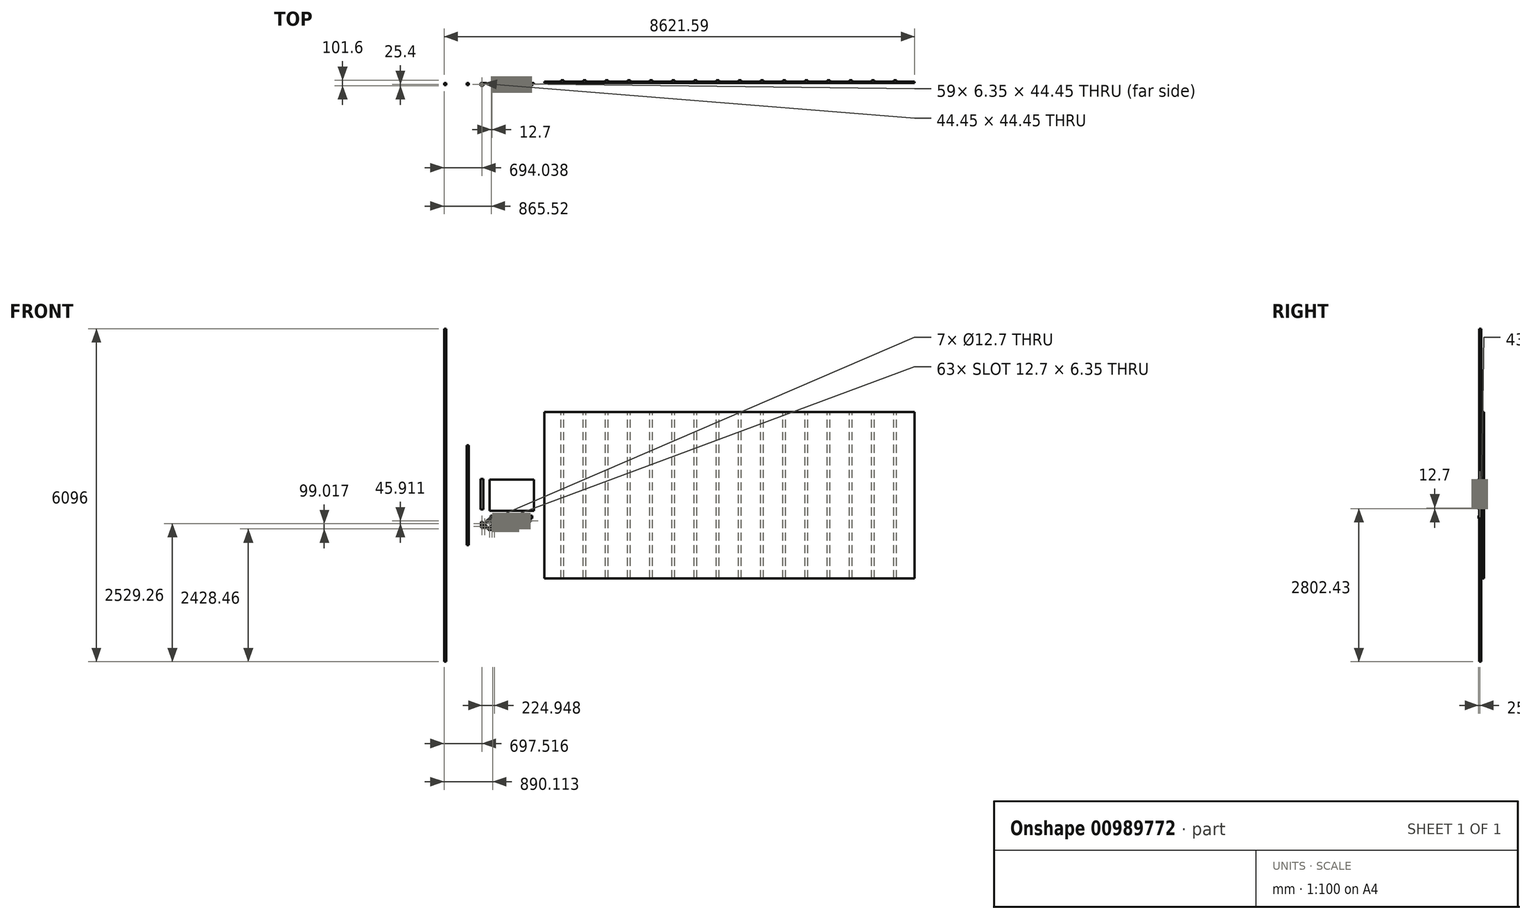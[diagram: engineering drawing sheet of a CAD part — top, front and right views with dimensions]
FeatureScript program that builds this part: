
annotation { "Feature Type Name" : "Feature", "Feature Type Description" : "" }
export const myFeature = defineFeature(function(context is Context, id is Id, definition is map)
    precondition{}
    {
        {
            var Q0;
            Q0=qCreatedBy(makeId("Front.planeOp"),FACE);
            var sketch = newSketch(context, id + "F0", { "sketchPlane" : qUnion([Q0])});
            skLineSegment(sketch, "E0.bottom", {"start": v(-3390.9, -1524) * mm, "end": v(3390.9, -1524) * mm});
            skLineSegment(sketch, "E0.top", {"start": v(-3390.9, 1524) * mm, "end": v(3390.9, 1524) * mm});
            skLineSegment(sketch, "E0.left", {"start": v(-3390.9, -1524) * mm, "end": v(-3390.9, 1524) * mm});
            skLineSegment(sketch, "E0.right", {"start": v(3390.9, -1524) * mm, "end": v(3390.9, 1524) * mm});
            skPoint(sketch, "E0.middle", {"position": v(0, 0) * mm});
            skSolve(sketch);
        }
        {
            var Q0;
            Q0 = qSketchRegion(id + "F0", true);
            extrude(context, id + "F1", {"entities" : qUnion([Q0]), "oppositeDirection" : true, "depth" : 25.4 * mm, "offsetDistance" : 25.4 * mm});
        }
        {
            var Q0;
            Q0=makeQuery(id+"F1.opExtrude","SWEPT_FACE",FACE,{"disambiguationData":[OSD([sQuery(id+"F0.wireOp",EDGE,"E0.top")])]});
            var sketch = newSketch(context, id + "F2", { "sketchPlane" : qUnion([Q0])});
            skLineSegment(sketch, "E1", {"start": v(-3390.9, 25.4) * mm, "end": v(-3086.1, 25.4) * mm});
            skLineSegment(sketch, "E2.bottom", {"start": v(-3086.1, 25.4) * mm, "end": v(-3060.7, 25.4) * mm});
            skLineSegment(sketch, "E2.top", {"start": v(-3086.1, 50.8) * mm, "end": v(-3060.7, 50.8) * mm});
            skLineSegment(sketch, "E2.left", {"start": v(-3086.1, 25.4) * mm, "end": v(-3086.1, 50.8) * mm});
            skLineSegment(sketch, "E2.right", {"start": v(-3060.7, 25.4) * mm, "end": v(-3060.7, 50.8) * mm});
            skLineSegment(sketch, "E3.MirrorCS", {"start": v(-3035.3, 50.8) * mm, "end": v(-3060.7, 50.8) * mm});
            skLineSegment(sketch, "E4.MirrorCS", {"start": v(-3035.3, 25.4) * mm, "end": v(-3035.3, 50.8) * mm});
            skLineSegment(sketch, "E5.MirrorCS", {"start": v(-3035.3, 25.4) * mm, "end": v(-3060.7, 25.4) * mm});
            skLineSegment(sketch, "E6.1.0.0", {"start": v(-2654.3, 25.4) * mm, "end": v(-2654.3, 50.8) * mm});
            skLineSegment(sketch, "E6.1.0.1", {"start": v(-2628.9, 25.4) * mm, "end": v(-2628.9, 50.8) * mm});
            skLineSegment(sketch, "E6.1.0.2", {"start": v(-2628.9, 50.8) * mm, "end": v(-2654.3, 50.8) * mm});
            skLineSegment(sketch, "E6.1.0.3", {"start": v(-2679.7, 50.8) * mm, "end": v(-2654.3, 50.8) * mm});
            skLineSegment(sketch, "E6.1.0.4", {"start": v(-2679.7, 25.4) * mm, "end": v(-2679.7, 50.8) * mm});
            skLineSegment(sketch, "E6.1.0.5", {"start": v(-2679.7, 25.4) * mm, "end": v(-2654.3, 25.4) * mm});
            skLineSegment(sketch, "E6.1.0.6", {"start": v(-2628.9, 25.4) * mm, "end": v(-2654.3, 25.4) * mm});
            skLineSegment(sketch, "E6.2.0.0", {"start": v(-2247.9, 25.4) * mm, "end": v(-2247.9, 50.8) * mm});
            skLineSegment(sketch, "E6.2.0.1", {"start": v(-2222.5, 25.4) * mm, "end": v(-2222.5, 50.8) * mm});
            skLineSegment(sketch, "E6.2.0.2", {"start": v(-2222.5, 50.8) * mm, "end": v(-2247.9, 50.8) * mm});
            skLineSegment(sketch, "E6.2.0.3", {"start": v(-2273.3, 50.8) * mm, "end": v(-2247.9, 50.8) * mm});
            skLineSegment(sketch, "E6.2.0.4", {"start": v(-2273.3, 25.4) * mm, "end": v(-2273.3, 50.8) * mm});
            skLineSegment(sketch, "E6.2.0.5", {"start": v(-2273.3, 25.4) * mm, "end": v(-2247.9, 25.4) * mm});
            skLineSegment(sketch, "E6.2.0.6", {"start": v(-2222.5, 25.4) * mm, "end": v(-2247.9, 25.4) * mm});
            skLineSegment(sketch, "E6.3.0.0", {"start": v(-1841.5, 25.4) * mm, "end": v(-1841.5, 50.8) * mm});
            skLineSegment(sketch, "E6.3.0.1", {"start": v(-1816.1, 25.4) * mm, "end": v(-1816.1, 50.8) * mm});
            skLineSegment(sketch, "E6.3.0.2", {"start": v(-1816.1, 50.8) * mm, "end": v(-1841.5, 50.8) * mm});
            skLineSegment(sketch, "E6.3.0.3", {"start": v(-1866.9, 50.8) * mm, "end": v(-1841.5, 50.8) * mm});
            skLineSegment(sketch, "E6.3.0.4", {"start": v(-1866.9, 25.4) * mm, "end": v(-1866.9, 50.8) * mm});
            skLineSegment(sketch, "E6.3.0.5", {"start": v(-1866.9, 25.4) * mm, "end": v(-1841.5, 25.4) * mm});
            skLineSegment(sketch, "E6.3.0.6", {"start": v(-1816.1, 25.4) * mm, "end": v(-1841.5, 25.4) * mm});
            skLineSegment(sketch, "E6.4.0.0", {"start": v(-1435.1, 25.4) * mm, "end": v(-1435.1, 50.8) * mm});
            skLineSegment(sketch, "E6.4.0.1", {"start": v(-1409.7, 25.4) * mm, "end": v(-1409.7, 50.8) * mm});
            skLineSegment(sketch, "E6.4.0.2", {"start": v(-1409.7, 50.8) * mm, "end": v(-1435.1, 50.8) * mm});
            skLineSegment(sketch, "E6.4.0.3", {"start": v(-1460.5, 50.8) * mm, "end": v(-1435.1, 50.8) * mm});
            skLineSegment(sketch, "E6.4.0.4", {"start": v(-1460.5, 25.4) * mm, "end": v(-1460.5, 50.8) * mm});
            skLineSegment(sketch, "E6.4.0.5", {"start": v(-1460.5, 25.4) * mm, "end": v(-1435.1, 25.4) * mm});
            skLineSegment(sketch, "E6.4.0.6", {"start": v(-1409.7, 25.4) * mm, "end": v(-1435.1, 25.4) * mm});
            skLineSegment(sketch, "E6.5.0.0", {"start": v(-1028.7, 25.4) * mm, "end": v(-1028.7, 50.8) * mm});
            skLineSegment(sketch, "E6.5.0.1", {"start": v(-1003.3, 25.4) * mm, "end": v(-1003.3, 50.8) * mm});
            skLineSegment(sketch, "E6.5.0.2", {"start": v(-1003.3, 50.8) * mm, "end": v(-1028.7, 50.8) * mm});
            skLineSegment(sketch, "E6.5.0.3", {"start": v(-1054.1, 50.8) * mm, "end": v(-1028.7, 50.8) * mm});
            skLineSegment(sketch, "E6.5.0.4", {"start": v(-1054.1, 25.4) * mm, "end": v(-1054.1, 50.8) * mm});
            skLineSegment(sketch, "E6.5.0.5", {"start": v(-1054.1, 25.4) * mm, "end": v(-1028.7, 25.4) * mm});
            skLineSegment(sketch, "E6.5.0.6", {"start": v(-1003.3, 25.4) * mm, "end": v(-1028.7, 25.4) * mm});
            skLineSegment(sketch, "E6.6.0.0", {"start": v(-622.3, 25.4) * mm, "end": v(-622.3, 50.8) * mm});
            skLineSegment(sketch, "E6.6.0.1", {"start": v(-596.9, 25.4) * mm, "end": v(-596.9, 50.8) * mm});
            skLineSegment(sketch, "E6.6.0.2", {"start": v(-596.9, 50.8) * mm, "end": v(-622.3, 50.8) * mm});
            skLineSegment(sketch, "E6.6.0.3", {"start": v(-647.7, 50.8) * mm, "end": v(-622.3, 50.8) * mm});
            skLineSegment(sketch, "E6.6.0.4", {"start": v(-647.7, 25.4) * mm, "end": v(-647.7, 50.8) * mm});
            skLineSegment(sketch, "E6.6.0.5", {"start": v(-647.7, 25.4) * mm, "end": v(-622.3, 25.4) * mm});
            skLineSegment(sketch, "E6.6.0.6", {"start": v(-596.9, 25.4) * mm, "end": v(-622.3, 25.4) * mm});
            skLineSegment(sketch, "E6.7.0.0", {"start": v(-215.9, 25.4) * mm, "end": v(-215.9, 50.8) * mm});
            skLineSegment(sketch, "E6.7.0.1", {"start": v(-190.5, 25.4) * mm, "end": v(-190.5, 50.8) * mm});
            skLineSegment(sketch, "E6.7.0.2", {"start": v(-190.5, 50.8) * mm, "end": v(-215.9, 50.8) * mm});
            skLineSegment(sketch, "E6.7.0.3", {"start": v(-241.3, 50.8) * mm, "end": v(-215.9, 50.8) * mm});
            skLineSegment(sketch, "E6.7.0.4", {"start": v(-241.3, 25.4) * mm, "end": v(-241.3, 50.8) * mm});
            skLineSegment(sketch, "E6.7.0.5", {"start": v(-241.3, 25.4) * mm, "end": v(-215.9, 25.4) * mm});
            skLineSegment(sketch, "E6.7.0.6", {"start": v(-190.5, 25.4) * mm, "end": v(-215.9, 25.4) * mm});
            skLineSegment(sketch, "E6.8.0.0", {"start": v(190.5, 25.4) * mm, "end": v(190.5, 50.8) * mm});
            skLineSegment(sketch, "E6.8.0.1", {"start": v(215.9, 25.4) * mm, "end": v(215.9, 50.8) * mm});
            skLineSegment(sketch, "E6.8.0.2", {"start": v(215.9, 50.8) * mm, "end": v(190.5, 50.8) * mm});
            skLineSegment(sketch, "E6.8.0.3", {"start": v(165.1, 50.8) * mm, "end": v(190.5, 50.8) * mm});
            skLineSegment(sketch, "E6.8.0.4", {"start": v(165.1, 25.4) * mm, "end": v(165.1, 50.8) * mm});
            skLineSegment(sketch, "E6.8.0.5", {"start": v(165.1, 25.4) * mm, "end": v(190.5, 25.4) * mm});
            skLineSegment(sketch, "E6.8.0.6", {"start": v(215.9, 25.4) * mm, "end": v(190.5, 25.4) * mm});
            skLineSegment(sketch, "E6.9.0.0", {"start": v(596.9, 25.4) * mm, "end": v(596.9, 50.8) * mm});
            skLineSegment(sketch, "E6.9.0.1", {"start": v(622.3, 25.4) * mm, "end": v(622.3, 50.8) * mm});
            skLineSegment(sketch, "E6.9.0.2", {"start": v(622.3, 50.8) * mm, "end": v(596.9, 50.8) * mm});
            skLineSegment(sketch, "E6.9.0.3", {"start": v(571.5, 50.8) * mm, "end": v(596.9, 50.8) * mm});
            skLineSegment(sketch, "E6.9.0.4", {"start": v(571.5, 25.4) * mm, "end": v(571.5, 50.8) * mm});
            skLineSegment(sketch, "E6.9.0.5", {"start": v(571.5, 25.4) * mm, "end": v(596.9, 25.4) * mm});
            skLineSegment(sketch, "E6.9.0.6", {"start": v(622.3, 25.4) * mm, "end": v(596.9, 25.4) * mm});
            skLineSegment(sketch, "E6.10.0.0", {"start": v(1003.3, 25.4) * mm, "end": v(1003.3, 50.8) * mm});
            skLineSegment(sketch, "E6.10.0.1", {"start": v(1028.7, 25.4) * mm, "end": v(1028.7, 50.8) * mm});
            skLineSegment(sketch, "E6.10.0.2", {"start": v(1028.7, 50.8) * mm, "end": v(1003.3, 50.8) * mm});
            skLineSegment(sketch, "E6.10.0.3", {"start": v(977.9, 50.8) * mm, "end": v(1003.3, 50.8) * mm});
            skLineSegment(sketch, "E6.10.0.4", {"start": v(977.9, 25.4) * mm, "end": v(977.9, 50.8) * mm});
            skLineSegment(sketch, "E6.10.0.5", {"start": v(977.9, 25.4) * mm, "end": v(1003.3, 25.4) * mm});
            skLineSegment(sketch, "E6.10.0.6", {"start": v(1028.7, 25.4) * mm, "end": v(1003.3, 25.4) * mm});
            skLineSegment(sketch, "E6.11.0.0", {"start": v(1409.7, 25.4) * mm, "end": v(1409.7, 50.8) * mm});
            skLineSegment(sketch, "E6.11.0.1", {"start": v(1435.1, 25.4) * mm, "end": v(1435.1, 50.8) * mm});
            skLineSegment(sketch, "E6.11.0.2", {"start": v(1435.1, 50.8) * mm, "end": v(1409.7, 50.8) * mm});
            skLineSegment(sketch, "E6.11.0.3", {"start": v(1384.3, 50.8) * mm, "end": v(1409.7, 50.8) * mm});
            skLineSegment(sketch, "E6.11.0.4", {"start": v(1384.3, 25.4) * mm, "end": v(1384.3, 50.8) * mm});
            skLineSegment(sketch, "E6.11.0.5", {"start": v(1384.3, 25.4) * mm, "end": v(1409.7, 25.4) * mm});
            skLineSegment(sketch, "E6.11.0.6", {"start": v(1435.1, 25.4) * mm, "end": v(1409.7, 25.4) * mm});
            skLineSegment(sketch, "E6.12.0.0", {"start": v(1816.1, 25.4) * mm, "end": v(1816.1, 50.8) * mm});
            skLineSegment(sketch, "E6.12.0.1", {"start": v(1841.5, 25.4) * mm, "end": v(1841.5, 50.8) * mm});
            skLineSegment(sketch, "E6.12.0.2", {"start": v(1841.5, 50.8) * mm, "end": v(1816.1, 50.8) * mm});
            skLineSegment(sketch, "E6.12.0.3", {"start": v(1790.7, 50.8) * mm, "end": v(1816.1, 50.8) * mm});
            skLineSegment(sketch, "E6.12.0.4", {"start": v(1790.7, 25.4) * mm, "end": v(1790.7, 50.8) * mm});
            skLineSegment(sketch, "E6.12.0.5", {"start": v(1790.7, 25.4) * mm, "end": v(1816.1, 25.4) * mm});
            skLineSegment(sketch, "E6.12.0.6", {"start": v(1841.5, 25.4) * mm, "end": v(1816.1, 25.4) * mm});
            skLineSegment(sketch, "E6.13.0.0", {"start": v(2222.5, 25.4) * mm, "end": v(2222.5, 50.8) * mm});
            skLineSegment(sketch, "E6.13.0.1", {"start": v(2247.9, 25.4) * mm, "end": v(2247.9, 50.8) * mm});
            skLineSegment(sketch, "E6.13.0.2", {"start": v(2247.9, 50.8) * mm, "end": v(2222.5, 50.8) * mm});
            skLineSegment(sketch, "E6.13.0.3", {"start": v(2197.1, 50.8) * mm, "end": v(2222.5, 50.8) * mm});
            skLineSegment(sketch, "E6.13.0.4", {"start": v(2197.1, 25.4) * mm, "end": v(2197.1, 50.8) * mm});
            skLineSegment(sketch, "E6.13.0.5", {"start": v(2197.1, 25.4) * mm, "end": v(2222.5, 25.4) * mm});
            skLineSegment(sketch, "E6.13.0.6", {"start": v(2247.9, 25.4) * mm, "end": v(2222.5, 25.4) * mm});
            skLineSegment(sketch, "E6.14.0.0", {"start": v(2628.9, 25.4) * mm, "end": v(2628.9, 50.8) * mm});
            skLineSegment(sketch, "E6.14.0.1", {"start": v(2654.3, 25.4) * mm, "end": v(2654.3, 50.8) * mm});
            skLineSegment(sketch, "E6.14.0.2", {"start": v(2654.3, 50.8) * mm, "end": v(2628.9, 50.8) * mm});
            skLineSegment(sketch, "E6.14.0.3", {"start": v(2603.5, 50.8) * mm, "end": v(2628.9, 50.8) * mm});
            skLineSegment(sketch, "E6.14.0.4", {"start": v(2603.5, 25.4) * mm, "end": v(2603.5, 50.8) * mm});
            skLineSegment(sketch, "E6.14.0.5", {"start": v(2603.5, 25.4) * mm, "end": v(2628.9, 25.4) * mm});
            skLineSegment(sketch, "E6.14.0.6", {"start": v(2654.3, 25.4) * mm, "end": v(2628.9, 25.4) * mm});
            skLineSegment(sketch, "E6.15.0.0", {"start": v(3035.3, 25.4) * mm, "end": v(3035.3, 50.8) * mm});
            skLineSegment(sketch, "E6.15.0.1", {"start": v(3060.7, 25.4) * mm, "end": v(3060.7, 50.8) * mm});
            skLineSegment(sketch, "E6.15.0.2", {"start": v(3060.7, 50.8) * mm, "end": v(3035.3, 50.8) * mm});
            skLineSegment(sketch, "E6.15.0.3", {"start": v(3009.9, 50.8) * mm, "end": v(3035.3, 50.8) * mm});
            skLineSegment(sketch, "E6.15.0.4", {"start": v(3009.9, 25.4) * mm, "end": v(3009.9, 50.8) * mm});
            skLineSegment(sketch, "E6.15.0.5", {"start": v(3009.9, 25.4) * mm, "end": v(3035.3, 25.4) * mm});
            skLineSegment(sketch, "E6.15.0.6", {"start": v(3060.7, 25.4) * mm, "end": v(3035.3, 25.4) * mm});
            skLineSegment(sketch, "E6.direction1", {"start": v(-3060.7, 25.4) * mm, "end": v(-2654.3, 25.4) * mm, "construction": true});
            skSolve(sketch);
        }
        {
            var Q0;
            Q0 = qSketchRegion(id + "F2", true);
            extrude(context, id + "F3", {"entities" : qUnion([Q0]), "operationType" : NewBodyOperationType.ADD, "oppositeDirection" : true, "depth" : 3048 * mm, "offsetDistance" : 25.4 * mm});
        }
        {
            var Q0;
            Q0=makeQuery(id+"F1.opExtrude","CAP_FACE",FACE,{"disambiguationData":[OSD([sQuery(id+"F0.wireOp",EDGE,"E0.bottom"),sQuery(id+"F0.wireOp",EDGE,"E0.top"),sQuery(id+"F0.wireOp",EDGE,"E0.left"),sQuery(id+"F0.wireOp",EDGE,"E0.right")])],"isStart":true});
            var sketch = newSketch(context, id + "F4", { "sketchPlane" : qUnion([Q0])});
            skLineSegment(sketch, "E7.bottom", {"start": v(-4398.38, -285.75) * mm, "end": v(-3585.58, -285.75) * mm});
            skLineSegment(sketch, "E7.top", {"start": v(-4398.38, 285.75) * mm, "end": v(-3585.58, 285.75) * mm});
            skLineSegment(sketch, "E7.left", {"start": v(-4398.38, -285.75) * mm, "end": v(-4398.38, 285.75) * mm});
            skLineSegment(sketch, "E7.right", {"start": v(-3585.58, -285.75) * mm, "end": v(-3585.58, 285.75) * mm});
            skPoint(sketch, "E7.middle", {"position": v(-3991.98, 0) * mm});
            skSolve(sketch);
        }
        {
            var Q0;
            Q0 = qSketchRegion(id + "F4", true);
            extrude(context, id + "F5", {"entities" : qUnion([Q0]), "depth" : 3.17 * mm, "offsetDistance" : 25.4 * mm});
        }
        {
            var Q0;
            Q0=makeQuery(id+"F1.opExtrude","CAP_FACE",FACE,{"disambiguationData":[OSD([sQuery(id+"F0.wireOp",EDGE,"E0.bottom"),sQuery(id+"F0.wireOp",EDGE,"E0.top"),sQuery(id+"F0.wireOp",EDGE,"E0.left"),sQuery(id+"F0.wireOp",EDGE,"E0.right")])],"isStart":true});
            var sketch = newSketch(context, id + "F6", { "sketchPlane" : qUnion([Q0])});
            skLineSegment(sketch, "E8.bottom", {"start": v(-4775.55, -914.4) * mm, "end": v(-4813.65, -914.4) * mm});
            skLineSegment(sketch, "E8.top", {"start": v(-4775.55, 914.4) * mm, "end": v(-4813.65, 914.4) * mm});
            skLineSegment(sketch, "E8.left", {"start": v(-4775.55, -914.4) * mm, "end": v(-4775.55, 914.4) * mm});
            skLineSegment(sketch, "E8.right", {"start": v(-4813.65, -914.4) * mm, "end": v(-4813.65, 914.4) * mm});
            skPoint(sketch, "E8.middle", {"position": v(-4794.6, 0) * mm});
            skLineSegment(sketch, "E9.bottom", {"start": v(-5192.6, -3048) * mm, "end": v(-5230.7, -3048) * mm});
            skLineSegment(sketch, "E9.top", {"start": v(-5192.6, 3048) * mm, "end": v(-5230.7, 3048) * mm});
            skLineSegment(sketch, "E9.left", {"start": v(-5192.6, -3048) * mm, "end": v(-5192.6, 3048) * mm});
            skLineSegment(sketch, "E9.right", {"start": v(-5230.7, -3048) * mm, "end": v(-5230.7, 3048) * mm});
            skPoint(sketch, "E9.middle", {"position": v(-5211.64, 0) * mm});
            skSolve(sketch);
        }
        {
            var Q0;
            Q0 = qSketchRegion(id + "F6", true);
            extrude(context, id + "F7", {"entities" : qUnion([Q0]), "depth" : 38.1 * mm, "offsetDistance" : 25.4 * mm});
        }
        {
            var Q0;
            Q0=makeQuery(id+"F1.opExtrude","CAP_FACE",FACE,{"disambiguationData":[OSD([sQuery(id+"F0.wireOp",EDGE,"E0.bottom"),sQuery(id+"F0.wireOp",EDGE,"E0.top"),sQuery(id+"F0.wireOp",EDGE,"E0.left"),sQuery(id+"F0.wireOp",EDGE,"E0.right")])],"isStart":true});
            var sketch = newSketch(context, id + "F8", { "sketchPlane" : qUnion([Q0])});
            skLineSegment(sketch, "E10.bottom", {"start": v(-4514.12, -590.37) * mm, "end": v(-4552.22, -590.37) * mm});
            skLineSegment(sketch, "E10.top", {"start": v(-4514.12, -488.77) * mm, "end": v(-4552.22, -488.77) * mm});
            skLineSegment(sketch, "E10.left", {"start": v(-4514.12, -590.37) * mm, "end": v(-4514.12, -488.77) * mm});
            skLineSegment(sketch, "E10.right", {"start": v(-4552.22, -590.37) * mm, "end": v(-4552.22, -488.77) * mm});
            skPoint(sketch, "E10.middle", {"position": v(-4533.17, -539.57) * mm});
            skLineSegment(sketch, "E11.bottom", {"start": v(-4282.83, -638.59) * mm, "end": v(-4422.53, -638.59) * mm});
            skLineSegment(sketch, "E11.top", {"start": v(-4282.83, -600.49) * mm, "end": v(-4422.53, -600.49) * mm});
            skLineSegment(sketch, "E11.left", {"start": v(-4282.83, -638.59) * mm, "end": v(-4282.83, -600.49) * mm});
            skLineSegment(sketch, "E11.right", {"start": v(-4422.53, -638.59) * mm, "end": v(-4422.53, -600.49) * mm});
            skPoint(sketch, "E11.middle", {"position": v(-4352.68, -619.54) * mm});
            skLineSegment(sketch, "E12.bottom", {"start": v(-4552.22, -590.37) * mm, "end": v(-4450.62, -590.37) * mm});
            skLineSegment(sketch, "E12.top", {"start": v(-4552.22, -552.27) * mm, "end": v(-4450.62, -552.27) * mm});
            skLineSegment(sketch, "E12.left", {"start": v(-4552.22, -590.37) * mm, "end": v(-4552.22, -552.27) * mm});
            skLineSegment(sketch, "E12.right", {"start": v(-4450.62, -590.37) * mm, "end": v(-4450.62, -552.27) * mm});
            skLineSegment(sketch, "E13.bottom", {"start": v(-4371.73, -638.59) * mm, "end": v(-4333.63, -638.59) * mm});
            skLineSegment(sketch, "E13.top", {"start": v(-4371.73, -549.69) * mm, "end": v(-4333.63, -549.69) * mm});
            skLineSegment(sketch, "E13.left", {"start": v(-4371.73, -638.59) * mm, "end": v(-4371.73, -549.69) * mm});
            skLineSegment(sketch, "E13.right", {"start": v(-4333.63, -638.59) * mm, "end": v(-4333.63, -549.69) * mm});
            skPoint(sketch, "E13.middle", {"position": v(-4352.68, -594.14) * mm});
            skSolve(sketch);
        }
        {
            var Q0;
            {var subQ0=sQuery(id+"F8.wireOp",EDGE,"E13.left");var subQ1=sQuery(id+"F8.wireOp",EDGE,"E11.bottom");var subQ2=makeQuery(id+"F8.imprint","INTERSECT",VERTEX,{"derivedFrom":[subQ1,subQ0]});var subQ11=sQuery(id+"F8.wireOp",EDGE,"E13.top");var subQ12=sQuery(id+"F8.wireOp",EDGE,"E11.right");var subQ13=sQuery(id+"F8.wireOp",EDGE,"E11.left");var subQ14=sQuery(id+"F8.wireOp",EDGE,"E10.bottom");var subQ18=sQuery(id+"F8.wireOp",EDGE,"E12.bottom");var subQ24=sQuery(id+"F8.wireOp",EDGE,"E10.top");Q0=qUnion([makeQuery(id+"F8.imprint","IMPRINT",FACE,{"disambiguationData":[TD([[makeQuery(id+"F8.imprint","IMPRINT",EDGE,{"derivedFrom":subQ24}),1.0]])]}),makeQuery(id+"F8.imprint","IMPRINT",FACE,{"disambiguationData":[TD([[makeQuery(id+"F8.imprint","IMPRINT",EDGE,{"derivedFrom":subQ18}),1.0]])]}),makeQuery(id+"F8.imprint","IMPRINT",FACE,{"disambiguationData":[TD([[makeQuery(id+"F8.imprint","IMPRINT",EDGE,{"derivedFrom":subQ14}),-1.0]])]}),makeQuery(id+"F8.imprint","IMPRINT",FACE,{"disambiguationData":[TD([[makeQuery(id+"F8.imprint","IMPRINT",EDGE,{"derivedFrom":subQ13}),1.0]])]}),makeQuery(id+"F8.imprint","IMPRINT",FACE,{"disambiguationData":[TD([[makeQuery(id+"F8.imprint","IMPRINT",EDGE,{"derivedFrom":subQ12}),-1.0]])]}),makeQuery(id+"F8.imprint","IMPRINT",FACE,{"disambiguationData":[TD([[makeQuery(id+"F8.imprint","IMPRINT",EDGE,{"derivedFrom":subQ11}),-1.0]])]}),makeQuery(id+"F8.imprint","IMPRINT",FACE,{"disambiguationData":[TD([[makeQuery(id+"F8.imprint","IMPRINT",EDGE,{"disambiguationData":[TD([[subQ2,1.0]])],"derivedFrom":subQ1}),-1.0]])]})]);}
            extrude(context, id + "F9", {"entities" : qUnion([Q0]), "depth" : 6.35 * mm, "offsetDistance" : 25.4 * mm});
        }
        {
            var Q0;
            Q0=makeQuery(id+"F9.opExtrude","CAP_FACE",FACE,{"disambiguationData":[OSD([sQuery(id+"F8.wireOp",EDGE,"E10.bottom"),sQuery(id+"F8.wireOp",EDGE,"E10.top"),sQuery(id+"F8.wireOp",EDGE,"E10.left"),sQuery(id+"F8.wireOp",EDGE,"E10.right"),sQuery(id+"F8.wireOp",EDGE,"E12.bottom"),sQuery(id+"F8.wireOp",EDGE,"E12.top"),sQuery(id+"F8.wireOp",EDGE,"E12.right")])],"isStart":false});
            var sketch = newSketch(context, id + "F10", { "sketchPlane" : qUnion([Q0])});
            skLineSegment(sketch, "E14", {"start": v(-4552.22, -590.37) * mm, "end": v(-4514.12, -552.27) * mm});
            skLineSegment(sketch, "E15", {"start": v(-4450.62, -571.32) * mm, "end": v(-4552.22, -571.32) * mm});
            skLineSegment(sketch, "E16", {"start": v(-4533.17, -488.77) * mm, "end": v(-4533.17, -590.37) * mm});
            skCircle(sketch, "E17", {"center": v(-4533.17, -520.52) * mm, "radius": 6.35 * mm});
            skPoint(sketch, "E17.centerSnap0", {"position": v(-4514.12, -520.52) * mm});
            skCircle(sketch, "E18", {"center": v(-4482.37, -571.32) * mm, "radius": 6.35 * mm});
            skPoint(sketch, "E18.centerSnap0", {"position": v(-4482.37, -552.27) * mm});
            skCircle(sketch, "E19", {"center": v(-4533.17, -571.32) * mm, "radius": 6.35 * mm});
            skSolve(sketch);
        }
        {
            var Q0;
            Q0 = qSketchRegion(id + "F10", true);
            extrude(context, id + "F11", {"entities" : qUnion([Q0]), "operationType" : NewBodyOperationType.REMOVE, "oppositeDirection" : true, "depth" : 25.4 * mm, "offsetDistance" : 25.4 * mm});
        }
        {
            var Q0;
            Q0=makeQuery(id+"F9.opExtrude","CAP_FACE",FACE,{"disambiguationData":[OSD([sQuery(id+"F8.wireOp",EDGE,"E11.bottom"),sQuery(id+"F8.wireOp",EDGE,"E11.top"),sQuery(id+"F8.wireOp",EDGE,"E11.left"),sQuery(id+"F8.wireOp",EDGE,"E11.right"),sQuery(id+"F8.wireOp",EDGE,"E13.top"),sQuery(id+"F8.wireOp",EDGE,"E13.left"),sQuery(id+"F8.wireOp",EDGE,"E13.right")])],"isStart":false});
            var sketch = newSketch(context, id + "F12", { "sketchPlane" : qUnion([Q0])});
            skCircle(sketch, "E20", {"center": v(-4352.68, -575.09) * mm, "radius": 6.35 * mm});
            skPoint(sketch, "E20.centerSnap0", {"position": v(-4352.68, -549.69) * mm});
            skPoint(sketch, "E20.centerSnap1", {"position": v(-4371.73, -575.09) * mm});
            skCircle(sketch, "E21", {"center": v(-4397.13, -619.54) * mm, "radius": 6.35 * mm});
            skPoint(sketch, "E21.centerSnap0", {"position": v(-4422.53, -619.54) * mm});
            skPoint(sketch, "E21.centerSnap1", {"position": v(-4397.13, -600.49) * mm});
            skCircle(sketch, "E22", {"center": v(-4308.23, -619.54) * mm, "radius": 6.35 * mm});
            skPoint(sketch, "E22.centerSnap0", {"position": v(-4282.83, -619.54) * mm});
            skPoint(sketch, "E22.centerSnap1", {"position": v(-4308.23, -600.49) * mm});
            skCircle(sketch, "E23", {"center": v(-4352.68, -619.54) * mm, "radius": 6.35 * mm});
            skPoint(sketch, "E23.centerSnap0", {"position": v(-4352.68, -638.59) * mm});
            skSolve(sketch);
        }
        {
            var Q0;
            Q0 = qSketchRegion(id + "F12", true);
            extrude(context, id + "F13", {"entities" : qUnion([Q0]), "operationType" : NewBodyOperationType.REMOVE, "oppositeDirection" : true, "depth" : 25.4 * mm, "offsetDistance" : 25.4 * mm});
        }
        {
            var Q0;
            Q0=makeQuery(id+"F1.opExtrude","CAP_FACE",FACE,{"disambiguationData":[OSD([sQuery(id+"F0.wireOp",EDGE,"E0.bottom"),sQuery(id+"F0.wireOp",EDGE,"E0.top"),sQuery(id+"F0.wireOp",EDGE,"E0.left"),sQuery(id+"F0.wireOp",EDGE,"E0.right")])],"isStart":true});
            var sketch = newSketch(context, id + "F14", { "sketchPlane" : qUnion([Q0])});
            skLineSegment(sketch, "E24.bottom", {"start": v(-4374.7, -372.24) * mm, "end": v(-3612.7, -372.24) * mm});
            skLineSegment(sketch, "E24.top", {"start": v(-4374.7, -423.04) * mm, "end": v(-3612.7, -423.04) * mm});
            skLineSegment(sketch, "E24.left", {"start": v(-4374.7, -372.24) * mm, "end": v(-4374.7, -423.04) * mm});
            skLineSegment(sketch, "E24.right", {"start": v(-3612.7, -372.24) * mm, "end": v(-3612.7, -423.04) * mm});
            skLineSegment(sketch, "E25.bottom", {"start": v(-4562.05, 297.36) * mm, "end": v(-4511.25, 297.36) * mm});
            skLineSegment(sketch, "E25.top", {"start": v(-4562.05, -261.44) * mm, "end": v(-4511.25, -261.44) * mm});
            skLineSegment(sketch, "E25.left", {"start": v(-4562.05, 297.36) * mm, "end": v(-4562.05, -261.44) * mm});
            skLineSegment(sketch, "E25.right", {"start": v(-4511.25, 297.36) * mm, "end": v(-4511.25, -261.44) * mm});
            skSolve(sketch);
        }
        {
            var Q0;
            Q0 = qSketchRegion(id + "F14", true);
            extrude(context, id + "F15", {"entities" : qUnion([Q0]), "depth" : 50.8 * mm, "offsetDistance" : 25.4 * mm});
        }
        {
            var Q0;
            Q0=makeQuery(id+"F15.opExtrude","SWEPT_FACE",FACE,{"disambiguationData":[OSD([sQuery(id+"F14.wireOp",EDGE,"E25.bottom")])]});
            var sketch = newSketch(context, id + "F16", { "sketchPlane" : qUnion([Q0])});
            skLineSegment(sketch, "E26.bottom", {"start": v(-4558.88, -3.18) * mm, "end": v(-4514.43, -3.18) * mm});
            skLineSegment(sketch, "E26.top", {"start": v(-4558.88, -47.63) * mm, "end": v(-4514.43, -47.63) * mm});
            skLineSegment(sketch, "E26.left", {"start": v(-4558.88, -3.18) * mm, "end": v(-4558.88, -47.63) * mm});
            skLineSegment(sketch, "E26.right", {"start": v(-4514.43, -3.18) * mm, "end": v(-4514.43, -47.63) * mm});
            skSolve(sketch);
        }
        {
            var Q0;
            Q0 = qSketchRegion(id + "F16", true);
            extrude(context, id + "F17", {"entities" : qUnion([Q0]), "operationType" : NewBodyOperationType.REMOVE, "oppositeDirection" : true, "depth" : 558.8 * mm, "offsetDistance" : 25.4 * mm});
        }
        {
            var Q0;
            Q0=makeQuery(id+"F15.opExtrude","SWEPT_FACE",FACE,{"disambiguationData":[OSD([sQuery(id+"F14.wireOp",EDGE,"E25.left")])]});
            var sketch = newSketch(context, id + "F18", { "sketchPlane" : qUnion([Q0])});
            skLineSegment(sketch, "E27.bottom", {"start": v(47.62, 291) * mm, "end": v(3.17, 291) * mm});
            skLineSegment(sketch, "E27.top", {"start": v(47.62, 284.66) * mm, "end": v(3.18, 284.66) * mm});
            skLineSegment(sketch, "E27.left", {"start": v(47.62, 284.66) * mm, "end": v(47.62, 291) * mm});
            skLineSegment(sketch, "E27.right", {"start": v(3.17, 284.66) * mm, "end": v(3.17, 291) * mm});
            skLineSegment(sketch, "E28.1.0.0", {"start": v(47.62, 271.96) * mm, "end": v(47.62, 278.3) * mm});
            skLineSegment(sketch, "E28.1.0.1", {"start": v(47.62, 271.96) * mm, "end": v(3.18, 271.96) * mm});
            skLineSegment(sketch, "E28.1.0.2", {"start": v(47.62, 278.3) * mm, "end": v(3.17, 278.3) * mm});
            skLineSegment(sketch, "E28.1.0.3", {"start": v(3.17, 271.96) * mm, "end": v(3.17, 278.3) * mm});
            skLineSegment(sketch, "E28.2.0.0", {"start": v(47.62, 259.26) * mm, "end": v(47.62, 265.6) * mm});
            skLineSegment(sketch, "E28.2.0.1", {"start": v(47.62, 259.26) * mm, "end": v(3.18, 259.26) * mm});
            skLineSegment(sketch, "E28.2.0.2", {"start": v(47.62, 265.6) * mm, "end": v(3.17, 265.6) * mm});
            skLineSegment(sketch, "E28.2.0.3", {"start": v(3.17, 259.26) * mm, "end": v(3.17, 265.6) * mm});
            skLineSegment(sketch, "E28.3.0.0", {"start": v(47.62, 246.56) * mm, "end": v(47.62, 252.9) * mm});
            skLineSegment(sketch, "E28.3.0.1", {"start": v(47.63, 246.56) * mm, "end": v(3.18, 246.56) * mm});
            skLineSegment(sketch, "E28.3.0.2", {"start": v(47.63, 252.9) * mm, "end": v(3.17, 252.9) * mm});
            skLineSegment(sketch, "E28.3.0.3", {"start": v(3.17, 246.56) * mm, "end": v(3.17, 252.9) * mm});
            skLineSegment(sketch, "E28.4.0.0", {"start": v(47.63, 233.86) * mm, "end": v(47.63, 240.2) * mm});
            skLineSegment(sketch, "E28.4.0.1", {"start": v(47.63, 233.86) * mm, "end": v(3.18, 233.86) * mm});
            skLineSegment(sketch, "E28.4.0.2", {"start": v(47.63, 240.2) * mm, "end": v(3.18, 240.2) * mm});
            skLineSegment(sketch, "E28.4.0.3", {"start": v(3.17, 233.86) * mm, "end": v(3.17, 240.2) * mm});
            skLineSegment(sketch, "E28.5.0.0", {"start": v(47.63, 221.16) * mm, "end": v(47.63, 227.5) * mm});
            skLineSegment(sketch, "E28.5.0.1", {"start": v(47.63, 221.16) * mm, "end": v(3.18, 221.16) * mm});
            skLineSegment(sketch, "E28.5.0.2", {"start": v(47.63, 227.5) * mm, "end": v(3.18, 227.5) * mm});
            skLineSegment(sketch, "E28.5.0.3", {"start": v(3.18, 221.16) * mm, "end": v(3.18, 227.5) * mm});
            skLineSegment(sketch, "E28.6.0.0", {"start": v(47.63, 208.46) * mm, "end": v(47.63, 214.8) * mm});
            skLineSegment(sketch, "E28.6.0.1", {"start": v(47.63, 208.46) * mm, "end": v(3.18, 208.46) * mm});
            skLineSegment(sketch, "E28.6.0.2", {"start": v(47.63, 214.8) * mm, "end": v(3.18, 214.8) * mm});
            skLineSegment(sketch, "E28.6.0.3", {"start": v(3.18, 208.46) * mm, "end": v(3.18, 214.8) * mm});
            skLineSegment(sketch, "E28.7.0.0", {"start": v(47.63, 195.76) * mm, "end": v(47.63, 202.1) * mm});
            skLineSegment(sketch, "E28.7.0.1", {"start": v(47.63, 195.76) * mm, "end": v(3.18, 195.76) * mm});
            skLineSegment(sketch, "E28.7.0.2", {"start": v(47.63, 202.1) * mm, "end": v(3.18, 202.1) * mm});
            skLineSegment(sketch, "E28.7.0.3", {"start": v(3.18, 195.76) * mm, "end": v(3.18, 202.1) * mm});
            skLineSegment(sketch, "E28.8.0.0", {"start": v(47.63, 183.06) * mm, "end": v(47.63, 189.4) * mm});
            skLineSegment(sketch, "E28.8.0.1", {"start": v(47.63, 183.06) * mm, "end": v(3.18, 183.06) * mm});
            skLineSegment(sketch, "E28.8.0.2", {"start": v(47.63, 189.4) * mm, "end": v(3.18, 189.4) * mm});
            skLineSegment(sketch, "E28.8.0.3", {"start": v(3.18, 183.06) * mm, "end": v(3.18, 189.4) * mm});
            skLineSegment(sketch, "E28.9.0.0", {"start": v(47.63, 170.36) * mm, "end": v(47.63, 176.7) * mm});
            skLineSegment(sketch, "E28.9.0.1", {"start": v(47.63, 170.36) * mm, "end": v(3.18, 170.36) * mm});
            skLineSegment(sketch, "E28.9.0.2", {"start": v(47.63, 176.7) * mm, "end": v(3.18, 176.7) * mm});
            skLineSegment(sketch, "E28.9.0.3", {"start": v(3.18, 170.36) * mm, "end": v(3.18, 176.7) * mm});
            skLineSegment(sketch, "E28.10.0.0", {"start": v(47.63, 157.66) * mm, "end": v(47.63, 164) * mm});
            skLineSegment(sketch, "E28.10.0.1", {"start": v(47.63, 157.66) * mm, "end": v(3.18, 157.66) * mm});
            skLineSegment(sketch, "E28.10.0.2", {"start": v(47.63, 164) * mm, "end": v(3.18, 164) * mm});
            skLineSegment(sketch, "E28.10.0.3", {"start": v(3.18, 157.66) * mm, "end": v(3.18, 164) * mm});
            skLineSegment(sketch, "E28.11.0.0", {"start": v(47.63, 144.96) * mm, "end": v(47.63, 151.3) * mm});
            skLineSegment(sketch, "E28.11.0.1", {"start": v(47.63, 144.96) * mm, "end": v(3.18, 144.96) * mm});
            skLineSegment(sketch, "E28.11.0.2", {"start": v(47.63, 151.3) * mm, "end": v(3.18, 151.3) * mm});
            skLineSegment(sketch, "E28.11.0.3", {"start": v(3.18, 144.96) * mm, "end": v(3.18, 151.3) * mm});
            skLineSegment(sketch, "E28.12.0.0", {"start": v(47.63, 132.26) * mm, "end": v(47.63, 138.6) * mm});
            skLineSegment(sketch, "E28.12.0.1", {"start": v(47.63, 132.26) * mm, "end": v(3.18, 132.26) * mm});
            skLineSegment(sketch, "E28.12.0.2", {"start": v(47.63, 138.6) * mm, "end": v(3.18, 138.6) * mm});
            skLineSegment(sketch, "E28.12.0.3", {"start": v(3.18, 132.26) * mm, "end": v(3.18, 138.6) * mm});
            skLineSegment(sketch, "E28.13.0.0", {"start": v(47.63, 119.56) * mm, "end": v(47.63, 125.9) * mm});
            skLineSegment(sketch, "E28.13.0.1", {"start": v(47.63, 119.56) * mm, "end": v(3.18, 119.56) * mm});
            skLineSegment(sketch, "E28.13.0.2", {"start": v(47.63, 125.9) * mm, "end": v(3.18, 125.9) * mm});
            skLineSegment(sketch, "E28.13.0.3", {"start": v(3.18, 119.56) * mm, "end": v(3.18, 125.9) * mm});
            skLineSegment(sketch, "E28.14.0.0", {"start": v(47.63, 106.86) * mm, "end": v(47.63, 113.2) * mm});
            skLineSegment(sketch, "E28.14.0.1", {"start": v(47.63, 106.86) * mm, "end": v(3.18, 106.86) * mm});
            skLineSegment(sketch, "E28.14.0.2", {"start": v(47.63, 113.2) * mm, "end": v(3.18, 113.2) * mm});
            skLineSegment(sketch, "E28.14.0.3", {"start": v(3.18, 106.86) * mm, "end": v(3.18, 113.2) * mm});
            skLineSegment(sketch, "E28.15.0.0", {"start": v(47.63, 94.16) * mm, "end": v(47.63, 100.5) * mm});
            skLineSegment(sketch, "E28.15.0.1", {"start": v(47.63, 94.16) * mm, "end": v(3.18, 94.16) * mm});
            skLineSegment(sketch, "E28.15.0.2", {"start": v(47.63, 100.5) * mm, "end": v(3.18, 100.5) * mm});
            skLineSegment(sketch, "E28.15.0.3", {"start": v(3.18, 94.16) * mm, "end": v(3.18, 100.5) * mm});
            skLineSegment(sketch, "E28.16.0.0", {"start": v(47.63, 81.46) * mm, "end": v(47.63, 87.8) * mm});
            skLineSegment(sketch, "E28.16.0.1", {"start": v(47.63, 81.46) * mm, "end": v(3.18, 81.46) * mm});
            skLineSegment(sketch, "E28.16.0.2", {"start": v(47.63, 87.8) * mm, "end": v(3.18, 87.8) * mm});
            skLineSegment(sketch, "E28.16.0.3", {"start": v(3.18, 81.46) * mm, "end": v(3.18, 87.8) * mm});
            skLineSegment(sketch, "E28.17.0.0", {"start": v(47.63, 68.76) * mm, "end": v(47.63, 75.1) * mm});
            skLineSegment(sketch, "E28.17.0.1", {"start": v(47.63, 68.76) * mm, "end": v(3.18, 68.76) * mm});
            skLineSegment(sketch, "E28.17.0.2", {"start": v(47.63, 75.1) * mm, "end": v(3.18, 75.1) * mm});
            skLineSegment(sketch, "E28.17.0.3", {"start": v(3.18, 68.76) * mm, "end": v(3.18, 75.1) * mm});
            skLineSegment(sketch, "E28.18.0.0", {"start": v(47.63, 56.06) * mm, "end": v(47.63, 62.4) * mm});
            skLineSegment(sketch, "E28.18.0.1", {"start": v(47.63, 56.06) * mm, "end": v(3.18, 56.06) * mm});
            skLineSegment(sketch, "E28.18.0.2", {"start": v(47.63, 62.4) * mm, "end": v(3.18, 62.4) * mm});
            skLineSegment(sketch, "E28.18.0.3", {"start": v(3.18, 56.06) * mm, "end": v(3.18, 62.4) * mm});
            skLineSegment(sketch, "E28.19.0.0", {"start": v(47.63, 43.36) * mm, "end": v(47.63, 49.7) * mm});
            skLineSegment(sketch, "E28.19.0.1", {"start": v(47.63, 43.36) * mm, "end": v(3.18, 43.36) * mm});
            skLineSegment(sketch, "E28.19.0.2", {"start": v(47.63, 49.7) * mm, "end": v(3.18, 49.7) * mm});
            skLineSegment(sketch, "E28.19.0.3", {"start": v(3.18, 43.36) * mm, "end": v(3.18, 49.7) * mm});
            skLineSegment(sketch, "E28.20.0.0", {"start": v(47.63, 30.66) * mm, "end": v(47.63, 37) * mm});
            skLineSegment(sketch, "E28.20.0.1", {"start": v(47.63, 30.66) * mm, "end": v(3.18, 30.66) * mm});
            skLineSegment(sketch, "E28.20.0.2", {"start": v(47.63, 37) * mm, "end": v(3.18, 37) * mm});
            skLineSegment(sketch, "E28.20.0.3", {"start": v(3.18, 30.66) * mm, "end": v(3.18, 37) * mm});
            skLineSegment(sketch, "E28.21.0.0", {"start": v(47.63, 17.96) * mm, "end": v(47.63, 24.3) * mm});
            skLineSegment(sketch, "E28.21.0.1", {"start": v(47.63, 17.96) * mm, "end": v(3.18, 17.96) * mm});
            skLineSegment(sketch, "E28.21.0.2", {"start": v(47.63, 24.3) * mm, "end": v(3.18, 24.3) * mm});
            skLineSegment(sketch, "E28.21.0.3", {"start": v(3.18, 17.96) * mm, "end": v(3.18, 24.3) * mm});
            skLineSegment(sketch, "E28.22.0.0", {"start": v(47.63, 5.26) * mm, "end": v(47.63, 11.6) * mm});
            skLineSegment(sketch, "E28.22.0.1", {"start": v(47.63, 5.26) * mm, "end": v(3.18, 5.26) * mm});
            skLineSegment(sketch, "E28.22.0.2", {"start": v(47.63, 11.6) * mm, "end": v(3.18, 11.6) * mm});
            skLineSegment(sketch, "E28.22.0.3", {"start": v(3.18, 5.26) * mm, "end": v(3.18, 11.6) * mm});
            skLineSegment(sketch, "E28.23.0.0", {"start": v(47.63, -7.44) * mm, "end": v(47.63, -1.1) * mm});
            skLineSegment(sketch, "E28.23.0.1", {"start": v(47.63, -7.44) * mm, "end": v(3.18, -7.44) * mm});
            skLineSegment(sketch, "E28.23.0.2", {"start": v(47.63, -1.1) * mm, "end": v(3.18, -1.1) * mm});
            skLineSegment(sketch, "E28.23.0.3", {"start": v(3.18, -7.44) * mm, "end": v(3.18, -1.1) * mm});
            skLineSegment(sketch, "E28.24.0.0", {"start": v(47.63, -20.14) * mm, "end": v(47.63, -13.8) * mm});
            skLineSegment(sketch, "E28.24.0.1", {"start": v(47.63, -20.14) * mm, "end": v(3.18, -20.14) * mm});
            skLineSegment(sketch, "E28.24.0.2", {"start": v(47.63, -13.8) * mm, "end": v(3.18, -13.8) * mm});
            skLineSegment(sketch, "E28.24.0.3", {"start": v(3.18, -20.14) * mm, "end": v(3.18, -13.8) * mm});
            skLineSegment(sketch, "E28.25.0.0", {"start": v(47.63, -32.84) * mm, "end": v(47.63, -26.5) * mm});
            skLineSegment(sketch, "E28.25.0.1", {"start": v(47.63, -32.84) * mm, "end": v(3.18, -32.84) * mm});
            skLineSegment(sketch, "E28.25.0.2", {"start": v(47.63, -26.5) * mm, "end": v(3.18, -26.5) * mm});
            skLineSegment(sketch, "E28.25.0.3", {"start": v(3.18, -32.84) * mm, "end": v(3.18, -26.5) * mm});
            skLineSegment(sketch, "E28.26.0.0", {"start": v(47.63, -45.54) * mm, "end": v(47.63, -39.2) * mm});
            skLineSegment(sketch, "E28.26.0.1", {"start": v(47.63, -45.54) * mm, "end": v(3.18, -45.54) * mm});
            skLineSegment(sketch, "E28.26.0.2", {"start": v(47.63, -39.2) * mm, "end": v(3.18, -39.2) * mm});
            skLineSegment(sketch, "E28.26.0.3", {"start": v(3.18, -45.54) * mm, "end": v(3.18, -39.2) * mm});
            skLineSegment(sketch, "E28.27.0.0", {"start": v(47.63, -58.24) * mm, "end": v(47.63, -51.9) * mm});
            skLineSegment(sketch, "E28.27.0.1", {"start": v(47.63, -58.24) * mm, "end": v(3.18, -58.24) * mm});
            skLineSegment(sketch, "E28.27.0.2", {"start": v(47.63, -51.9) * mm, "end": v(3.18, -51.9) * mm});
            skLineSegment(sketch, "E28.27.0.3", {"start": v(3.18, -58.24) * mm, "end": v(3.18, -51.9) * mm});
            skLineSegment(sketch, "E28.28.0.0", {"start": v(47.63, -70.94) * mm, "end": v(47.63, -64.6) * mm});
            skLineSegment(sketch, "E28.28.0.1", {"start": v(47.63, -70.94) * mm, "end": v(3.18, -70.94) * mm});
            skLineSegment(sketch, "E28.28.0.2", {"start": v(47.63, -64.6) * mm, "end": v(3.18, -64.6) * mm});
            skLineSegment(sketch, "E28.28.0.3", {"start": v(3.18, -70.94) * mm, "end": v(3.18, -64.6) * mm});
            skLineSegment(sketch, "E28.29.0.0", {"start": v(47.63, -83.64) * mm, "end": v(47.63, -77.3) * mm});
            skLineSegment(sketch, "E28.29.0.1", {"start": v(47.63, -83.64) * mm, "end": v(3.18, -83.64) * mm});
            skLineSegment(sketch, "E28.29.0.2", {"start": v(47.63, -77.3) * mm, "end": v(3.18, -77.3) * mm});
            skLineSegment(sketch, "E28.29.0.3", {"start": v(3.18, -83.64) * mm, "end": v(3.18, -77.3) * mm});
            skLineSegment(sketch, "E28.30.0.0", {"start": v(47.63, -96.34) * mm, "end": v(47.63, -90) * mm});
            skLineSegment(sketch, "E28.30.0.1", {"start": v(47.63, -96.34) * mm, "end": v(3.18, -96.34) * mm});
            skLineSegment(sketch, "E28.30.0.2", {"start": v(47.63, -90) * mm, "end": v(3.18, -90) * mm});
            skLineSegment(sketch, "E28.30.0.3", {"start": v(3.18, -96.34) * mm, "end": v(3.18, -90) * mm});
            skLineSegment(sketch, "E28.31.0.0", {"start": v(47.63, -109.04) * mm, "end": v(47.63, -102.7) * mm});
            skLineSegment(sketch, "E28.31.0.1", {"start": v(47.63, -109.04) * mm, "end": v(3.18, -109.04) * mm});
            skLineSegment(sketch, "E28.31.0.2", {"start": v(47.63, -102.7) * mm, "end": v(3.18, -102.7) * mm});
            skLineSegment(sketch, "E28.31.0.3", {"start": v(3.18, -109.04) * mm, "end": v(3.18, -102.7) * mm});
            skLineSegment(sketch, "E28.32.0.0", {"start": v(47.63, -121.74) * mm, "end": v(47.63, -115.4) * mm});
            skLineSegment(sketch, "E28.32.0.1", {"start": v(47.63, -121.74) * mm, "end": v(3.18, -121.74) * mm});
            skLineSegment(sketch, "E28.32.0.2", {"start": v(47.63, -115.4) * mm, "end": v(3.18, -115.4) * mm});
            skLineSegment(sketch, "E28.32.0.3", {"start": v(3.18, -121.74) * mm, "end": v(3.18, -115.4) * mm});
            skLineSegment(sketch, "E28.33.0.0", {"start": v(47.63, -134.44) * mm, "end": v(47.63, -128.1) * mm});
            skLineSegment(sketch, "E28.33.0.1", {"start": v(47.63, -134.44) * mm, "end": v(3.18, -134.44) * mm});
            skLineSegment(sketch, "E28.33.0.2", {"start": v(47.63, -128.1) * mm, "end": v(3.18, -128.1) * mm});
            skLineSegment(sketch, "E28.33.0.3", {"start": v(3.18, -134.44) * mm, "end": v(3.18, -128.1) * mm});
            skLineSegment(sketch, "E28.34.0.0", {"start": v(47.63, -147.14) * mm, "end": v(47.63, -140.8) * mm});
            skLineSegment(sketch, "E28.34.0.1", {"start": v(47.63, -147.14) * mm, "end": v(3.18, -147.14) * mm});
            skLineSegment(sketch, "E28.34.0.2", {"start": v(47.63, -140.8) * mm, "end": v(3.18, -140.8) * mm});
            skLineSegment(sketch, "E28.34.0.3", {"start": v(3.18, -147.14) * mm, "end": v(3.18, -140.8) * mm});
            skLineSegment(sketch, "E28.35.0.0", {"start": v(47.63, -159.84) * mm, "end": v(47.63, -153.5) * mm});
            skLineSegment(sketch, "E28.35.0.1", {"start": v(47.63, -159.84) * mm, "end": v(3.18, -159.84) * mm});
            skLineSegment(sketch, "E28.35.0.2", {"start": v(47.63, -153.5) * mm, "end": v(3.18, -153.5) * mm});
            skLineSegment(sketch, "E28.35.0.3", {"start": v(3.18, -159.84) * mm, "end": v(3.18, -153.5) * mm});
            skLineSegment(sketch, "E28.36.0.0", {"start": v(47.63, -172.54) * mm, "end": v(47.63, -166.2) * mm});
            skLineSegment(sketch, "E28.36.0.1", {"start": v(47.63, -172.54) * mm, "end": v(3.18, -172.54) * mm});
            skLineSegment(sketch, "E28.36.0.2", {"start": v(47.63, -166.2) * mm, "end": v(3.18, -166.2) * mm});
            skLineSegment(sketch, "E28.36.0.3", {"start": v(3.18, -172.54) * mm, "end": v(3.18, -166.2) * mm});
            skLineSegment(sketch, "E28.37.0.0", {"start": v(47.63, -185.24) * mm, "end": v(47.63, -178.9) * mm});
            skLineSegment(sketch, "E28.37.0.1", {"start": v(47.63, -185.24) * mm, "end": v(3.18, -185.24) * mm});
            skLineSegment(sketch, "E28.37.0.2", {"start": v(47.63, -178.9) * mm, "end": v(3.18, -178.9) * mm});
            skLineSegment(sketch, "E28.37.0.3", {"start": v(3.18, -185.24) * mm, "end": v(3.18, -178.9) * mm});
            skLineSegment(sketch, "E28.38.0.0", {"start": v(47.63, -197.94) * mm, "end": v(47.63, -191.6) * mm});
            skLineSegment(sketch, "E28.38.0.1", {"start": v(47.63, -197.94) * mm, "end": v(3.18, -197.94) * mm});
            skLineSegment(sketch, "E28.38.0.2", {"start": v(47.63, -191.6) * mm, "end": v(3.18, -191.6) * mm});
            skLineSegment(sketch, "E28.38.0.3", {"start": v(3.18, -197.94) * mm, "end": v(3.18, -191.6) * mm});
            skLineSegment(sketch, "E28.39.0.0", {"start": v(47.63, -210.64) * mm, "end": v(47.63, -204.3) * mm});
            skLineSegment(sketch, "E28.39.0.1", {"start": v(47.63, -210.64) * mm, "end": v(3.18, -210.64) * mm});
            skLineSegment(sketch, "E28.39.0.2", {"start": v(47.63, -204.3) * mm, "end": v(3.18, -204.3) * mm});
            skLineSegment(sketch, "E28.39.0.3", {"start": v(3.18, -210.64) * mm, "end": v(3.18, -204.3) * mm});
            skLineSegment(sketch, "E28.direction1", {"start": v(47.62, 284.66) * mm, "end": v(47.62, 271.96) * mm, "construction": true});
            skLineSegment(sketch, "E29.0.40.0", {"start": v(47.63, -223.34) * mm, "end": v(47.63, -217) * mm});
            skLineSegment(sketch, "E29.3.40.0", {"start": v(47.63, -223.34) * mm, "end": v(3.18, -223.34) * mm});
            skLineSegment(sketch, "E29.6.40.0", {"start": v(47.63, -217) * mm, "end": v(3.18, -217) * mm});
            skLineSegment(sketch, "E29.9.40.0", {"start": v(3.18, -223.34) * mm, "end": v(3.18, -217) * mm});
            skLineSegment(sketch, "E30.0.41.0", {"start": v(47.63, -236.04) * mm, "end": v(47.63, -229.7) * mm});
            skLineSegment(sketch, "E30.3.41.0", {"start": v(47.63, -236.04) * mm, "end": v(3.18, -236.04) * mm});
            skLineSegment(sketch, "E30.6.41.0", {"start": v(47.63, -229.7) * mm, "end": v(3.18, -229.7) * mm});
            skLineSegment(sketch, "E30.9.41.0", {"start": v(3.18, -236.04) * mm, "end": v(3.18, -229.7) * mm});
            skLineSegment(sketch, "E30.0.42.0", {"start": v(47.63, -248.74) * mm, "end": v(47.63, -242.4) * mm});
            skLineSegment(sketch, "E30.3.42.0", {"start": v(47.63, -248.74) * mm, "end": v(3.18, -248.74) * mm});
            skLineSegment(sketch, "E30.6.42.0", {"start": v(47.63, -242.4) * mm, "end": v(3.18, -242.4) * mm});
            skLineSegment(sketch, "E30.9.42.0", {"start": v(3.18, -248.74) * mm, "end": v(3.18, -242.4) * mm});
            skLineSegment(sketch, "E30.0.43.0", {"start": v(47.63, -261.44) * mm, "end": v(47.63, -255.1) * mm});
            skLineSegment(sketch, "E30.3.43.0", {"start": v(47.63, -261.44) * mm, "end": v(3.18, -261.44) * mm});
            skLineSegment(sketch, "E30.6.43.0", {"start": v(47.63, -255.1) * mm, "end": v(3.18, -255.1) * mm});
            skLineSegment(sketch, "E30.9.43.0", {"start": v(3.18, -261.44) * mm, "end": v(3.18, -255.1) * mm});
            skSolve(sketch);
        }
        {
            var Q0;
            Q0=makeQuery(id+"F18.imprint","IMPRINT",FACE,{"disambiguationData":[TD([[makeQuery(id+"F18.imprint","IMPRINT",EDGE,{"derivedFrom":sQuery(id+"F18.wireOp",EDGE,"E27.bottom")}),1.0]])]});
            var Q1;
            Q1=makeQuery(id+"F18.imprint","IMPRINT",FACE,{"disambiguationData":[TD([[makeQuery(id+"F18.imprint","IMPRINT",EDGE,{"derivedFrom":sQuery(id+"F18.wireOp",EDGE,"E28.1.0.0")}),1.0]])]});
            var Q2;
            Q2=makeQuery(id+"F18.imprint","IMPRINT",FACE,{"disambiguationData":[TD([[makeQuery(id+"F18.imprint","IMPRINT",EDGE,{"derivedFrom":sQuery(id+"F18.wireOp",EDGE,"E28.2.0.0")}),1.0]])]});
            var Q3;
            Q3=makeQuery(id+"F18.imprint","IMPRINT",FACE,{"disambiguationData":[TD([[makeQuery(id+"F18.imprint","IMPRINT",EDGE,{"derivedFrom":sQuery(id+"F18.wireOp",EDGE,"E28.3.0.0")}),1.0]])]});
            var Q4;
            Q4=makeQuery(id+"F18.imprint","IMPRINT",FACE,{"disambiguationData":[TD([[makeQuery(id+"F18.imprint","IMPRINT",EDGE,{"derivedFrom":sQuery(id+"F18.wireOp",EDGE,"E28.4.0.0")}),1.0]])]});
            var Q5;
            Q5=makeQuery(id+"F18.imprint","IMPRINT",FACE,{"disambiguationData":[TD([[makeQuery(id+"F18.imprint","IMPRINT",EDGE,{"derivedFrom":sQuery(id+"F18.wireOp",EDGE,"E28.5.0.0")}),1.0]])]});
            var Q6;
            Q6=makeQuery(id+"F18.imprint","IMPRINT",FACE,{"disambiguationData":[TD([[makeQuery(id+"F18.imprint","IMPRINT",EDGE,{"derivedFrom":sQuery(id+"F18.wireOp",EDGE,"E28.6.0.0")}),1.0]])]});
            var Q7;
            Q7=makeQuery(id+"F18.imprint","IMPRINT",FACE,{"disambiguationData":[TD([[makeQuery(id+"F18.imprint","IMPRINT",EDGE,{"derivedFrom":sQuery(id+"F18.wireOp",EDGE,"E28.7.0.0")}),1.0]])]});
            var Q8;
            Q8=makeQuery(id+"F18.imprint","IMPRINT",FACE,{"disambiguationData":[TD([[makeQuery(id+"F18.imprint","IMPRINT",EDGE,{"derivedFrom":sQuery(id+"F18.wireOp",EDGE,"E28.8.0.0")}),1.0]])]});
            var Q9;
            Q9=makeQuery(id+"F18.imprint","IMPRINT",FACE,{"disambiguationData":[TD([[makeQuery(id+"F18.imprint","IMPRINT",EDGE,{"derivedFrom":sQuery(id+"F18.wireOp",EDGE,"E28.9.0.0")}),1.0]])]});
            var Q10;
            Q10=makeQuery(id+"F18.imprint","IMPRINT",FACE,{"disambiguationData":[TD([[makeQuery(id+"F18.imprint","IMPRINT",EDGE,{"derivedFrom":sQuery(id+"F18.wireOp",EDGE,"E28.10.0.0")}),1.0]])]});
            var Q11;
            Q11=makeQuery(id+"F18.imprint","IMPRINT",FACE,{"disambiguationData":[TD([[makeQuery(id+"F18.imprint","IMPRINT",EDGE,{"derivedFrom":sQuery(id+"F18.wireOp",EDGE,"E28.11.0.0")}),1.0]])]});
            var Q12;
            Q12=makeQuery(id+"F18.imprint","IMPRINT",FACE,{"disambiguationData":[TD([[makeQuery(id+"F18.imprint","IMPRINT",EDGE,{"derivedFrom":sQuery(id+"F18.wireOp",EDGE,"E28.12.0.0")}),1.0]])]});
            var Q13;
            Q13=makeQuery(id+"F18.imprint","IMPRINT",FACE,{"disambiguationData":[TD([[makeQuery(id+"F18.imprint","IMPRINT",EDGE,{"derivedFrom":sQuery(id+"F18.wireOp",EDGE,"E28.13.0.0")}),1.0]])]});
            var Q14;
            Q14=makeQuery(id+"F18.imprint","IMPRINT",FACE,{"disambiguationData":[TD([[makeQuery(id+"F18.imprint","IMPRINT",EDGE,{"derivedFrom":sQuery(id+"F18.wireOp",EDGE,"E28.14.0.0")}),1.0]])]});
            var Q15;
            Q15=makeQuery(id+"F18.imprint","IMPRINT",FACE,{"disambiguationData":[TD([[makeQuery(id+"F18.imprint","IMPRINT",EDGE,{"derivedFrom":sQuery(id+"F18.wireOp",EDGE,"E28.15.0.0")}),1.0]])]});
            var Q16;
            Q16=makeQuery(id+"F18.imprint","IMPRINT",FACE,{"disambiguationData":[TD([[makeQuery(id+"F18.imprint","IMPRINT",EDGE,{"derivedFrom":sQuery(id+"F18.wireOp",EDGE,"E28.16.0.0")}),1.0]])]});
            var Q17;
            Q17=makeQuery(id+"F18.imprint","IMPRINT",FACE,{"disambiguationData":[TD([[makeQuery(id+"F18.imprint","IMPRINT",EDGE,{"derivedFrom":sQuery(id+"F18.wireOp",EDGE,"E28.17.0.0")}),1.0]])]});
            var Q18;
            Q18=makeQuery(id+"F18.imprint","IMPRINT",FACE,{"disambiguationData":[TD([[makeQuery(id+"F18.imprint","IMPRINT",EDGE,{"derivedFrom":sQuery(id+"F18.wireOp",EDGE,"E28.18.0.0")}),1.0]])]});
            var Q19;
            Q19=makeQuery(id+"F18.imprint","IMPRINT",FACE,{"disambiguationData":[TD([[makeQuery(id+"F18.imprint","IMPRINT",EDGE,{"derivedFrom":sQuery(id+"F18.wireOp",EDGE,"E28.19.0.0")}),1.0]])]});
            var Q20;
            Q20=makeQuery(id+"F18.imprint","IMPRINT",FACE,{"disambiguationData":[TD([[makeQuery(id+"F18.imprint","IMPRINT",EDGE,{"derivedFrom":sQuery(id+"F18.wireOp",EDGE,"E28.20.0.0")}),1.0]])]});
            var Q21;
            Q21=makeQuery(id+"F18.imprint","IMPRINT",FACE,{"disambiguationData":[TD([[makeQuery(id+"F18.imprint","IMPRINT",EDGE,{"derivedFrom":sQuery(id+"F18.wireOp",EDGE,"E28.21.0.0")}),1.0]])]});
            var Q22;
            Q22=makeQuery(id+"F18.imprint","IMPRINT",FACE,{"disambiguationData":[TD([[makeQuery(id+"F18.imprint","IMPRINT",EDGE,{"derivedFrom":sQuery(id+"F18.wireOp",EDGE,"E28.22.0.0")}),1.0]])]});
            var Q23;
            Q23=makeQuery(id+"F18.imprint","IMPRINT",FACE,{"disambiguationData":[TD([[makeQuery(id+"F18.imprint","IMPRINT",EDGE,{"derivedFrom":sQuery(id+"F18.wireOp",EDGE,"E28.23.0.0")}),1.0]])]});
            var Q24;
            Q24=makeQuery(id+"F18.imprint","IMPRINT",FACE,{"disambiguationData":[TD([[makeQuery(id+"F18.imprint","IMPRINT",EDGE,{"derivedFrom":sQuery(id+"F18.wireOp",EDGE,"E28.24.0.0")}),1.0]])]});
            var Q25;
            Q25=makeQuery(id+"F18.imprint","IMPRINT",FACE,{"disambiguationData":[TD([[makeQuery(id+"F18.imprint","IMPRINT",EDGE,{"derivedFrom":sQuery(id+"F18.wireOp",EDGE,"E28.25.0.0")}),1.0]])]});
            var Q26;
            Q26=makeQuery(id+"F18.imprint","IMPRINT",FACE,{"disambiguationData":[TD([[makeQuery(id+"F18.imprint","IMPRINT",EDGE,{"derivedFrom":sQuery(id+"F18.wireOp",EDGE,"E28.26.0.0")}),1.0]])]});
            var Q27;
            Q27=makeQuery(id+"F18.imprint","IMPRINT",FACE,{"disambiguationData":[TD([[makeQuery(id+"F18.imprint","IMPRINT",EDGE,{"derivedFrom":sQuery(id+"F18.wireOp",EDGE,"E28.27.0.0")}),1.0]])]});
            var Q28;
            Q28=makeQuery(id+"F18.imprint","IMPRINT",FACE,{"disambiguationData":[TD([[makeQuery(id+"F18.imprint","IMPRINT",EDGE,{"derivedFrom":sQuery(id+"F18.wireOp",EDGE,"E28.28.0.0")}),1.0]])]});
            var Q29;
            Q29=makeQuery(id+"F18.imprint","IMPRINT",FACE,{"disambiguationData":[TD([[makeQuery(id+"F18.imprint","IMPRINT",EDGE,{"derivedFrom":sQuery(id+"F18.wireOp",EDGE,"E28.29.0.0")}),1.0]])]});
            var Q30;
            Q30=makeQuery(id+"F18.imprint","IMPRINT",FACE,{"disambiguationData":[TD([[makeQuery(id+"F18.imprint","IMPRINT",EDGE,{"derivedFrom":sQuery(id+"F18.wireOp",EDGE,"E28.30.0.0")}),1.0]])]});
            var Q31;
            Q31=makeQuery(id+"F18.imprint","IMPRINT",FACE,{"disambiguationData":[TD([[makeQuery(id+"F18.imprint","IMPRINT",EDGE,{"derivedFrom":sQuery(id+"F18.wireOp",EDGE,"E28.31.0.0")}),1.0]])]});
            var Q32;
            Q32=makeQuery(id+"F18.imprint","IMPRINT",FACE,{"disambiguationData":[TD([[makeQuery(id+"F18.imprint","IMPRINT",EDGE,{"derivedFrom":sQuery(id+"F18.wireOp",EDGE,"E28.32.0.0")}),1.0]])]});
            var Q33;
            Q33=makeQuery(id+"F18.imprint","IMPRINT",FACE,{"disambiguationData":[TD([[makeQuery(id+"F18.imprint","IMPRINT",EDGE,{"derivedFrom":sQuery(id+"F18.wireOp",EDGE,"E28.33.0.0")}),1.0]])]});
            var Q34;
            Q34=makeQuery(id+"F18.imprint","IMPRINT",FACE,{"disambiguationData":[TD([[makeQuery(id+"F18.imprint","IMPRINT",EDGE,{"derivedFrom":sQuery(id+"F18.wireOp",EDGE,"E28.34.0.0")}),1.0]])]});
            var Q35;
            Q35=makeQuery(id+"F18.imprint","IMPRINT",FACE,{"disambiguationData":[TD([[makeQuery(id+"F18.imprint","IMPRINT",EDGE,{"derivedFrom":sQuery(id+"F18.wireOp",EDGE,"E28.35.0.0")}),1.0]])]});
            var Q36;
            Q36=makeQuery(id+"F18.imprint","IMPRINT",FACE,{"disambiguationData":[TD([[makeQuery(id+"F18.imprint","IMPRINT",EDGE,{"derivedFrom":sQuery(id+"F18.wireOp",EDGE,"E28.36.0.0")}),1.0]])]});
            var Q37;
            Q37=makeQuery(id+"F18.imprint","IMPRINT",FACE,{"disambiguationData":[TD([[makeQuery(id+"F18.imprint","IMPRINT",EDGE,{"derivedFrom":sQuery(id+"F18.wireOp",EDGE,"E28.37.0.0")}),1.0]])]});
            var Q38;
            Q38=makeQuery(id+"F18.imprint","IMPRINT",FACE,{"disambiguationData":[TD([[makeQuery(id+"F18.imprint","IMPRINT",EDGE,{"derivedFrom":sQuery(id+"F18.wireOp",EDGE,"E28.38.0.0")}),1.0]])]});
            var Q39;
            Q39=makeQuery(id+"F18.imprint","IMPRINT",FACE,{"disambiguationData":[TD([[makeQuery(id+"F18.imprint","IMPRINT",EDGE,{"derivedFrom":sQuery(id+"F18.wireOp",EDGE,"E28.39.0.0")}),1.0]])]});
            var Q40;
            Q40=makeQuery(id+"F18.imprint","IMPRINT",FACE,{"disambiguationData":[TD([[makeQuery(id+"F18.imprint","IMPRINT",EDGE,{"derivedFrom":sQuery(id+"F18.wireOp",EDGE,"E29.0.40.0")}),1.0]])]});
            var Q41;
            Q41=makeQuery(id+"F18.imprint","IMPRINT",FACE,{"disambiguationData":[TD([[makeQuery(id+"F18.imprint","IMPRINT",EDGE,{"derivedFrom":sQuery(id+"F18.wireOp",EDGE,"E30.0.41.0")}),1.0]])]});
            var Q42;
            Q42=makeQuery(id+"F18.imprint","IMPRINT",FACE,{"disambiguationData":[TD([[makeQuery(id+"F18.imprint","IMPRINT",EDGE,{"derivedFrom":sQuery(id+"F18.wireOp",EDGE,"E30.0.42.0")}),1.0]])]});
            extrude(context, id + "F19", {"entities" : qUnion([Q0, Q1, Q2, Q3, Q4, Q5, Q6, Q7, Q8, Q9, Q10, Q11, Q12, Q13, Q14, Q15, Q16, Q17, Q18, Q19, Q20, Q21, Q22, Q23, Q24, Q25, Q26, Q27, Q28, Q29, Q30, Q31, Q32, Q33, Q34, Q35, Q36, Q37, Q38, Q39, Q40, Q41, Q42]), "operationType" : NewBodyOperationType.REMOVE, "oppositeDirection" : true, "depth" : 50.8 * mm, "offsetDistance" : 25.4 * mm});
        }
        {
            var Q0;
            Q0=makeQuery(id+"F15.opExtrude","SWEPT_FACE",FACE,{"disambiguationData":[OSD([sQuery(id+"F14.wireOp",EDGE,"E24.top")])]});
            var sketch = newSketch(context, id + "F20", { "sketchPlane" : qUnion([Q0])});
            skLineSegment(sketch, "E31.bottom", {"start": v(-4368.34, 47.63) * mm, "end": v(-4362, 47.63) * mm});
            skLineSegment(sketch, "E31.top", {"start": v(-4368.34, 3.18) * mm, "end": v(-4362, 3.18) * mm});
            skLineSegment(sketch, "E31.left", {"start": v(-4368.34, 47.63) * mm, "end": v(-4368.34, 3.18) * mm});
            skLineSegment(sketch, "E31.right", {"start": v(-4362, 47.63) * mm, "end": v(-4362, 3.18) * mm});
            skLineSegment(sketch, "E32.1.0.0", {"start": v(-4355.64, 47.63) * mm, "end": v(-4349.3, 47.63) * mm});
            skLineSegment(sketch, "E32.1.0.1", {"start": v(-4349.3, 47.63) * mm, "end": v(-4349.3, 3.18) * mm});
            skLineSegment(sketch, "E32.1.0.2", {"start": v(-4355.64, 47.63) * mm, "end": v(-4355.64, 3.18) * mm});
            skLineSegment(sketch, "E32.1.0.3", {"start": v(-4355.64, 3.18) * mm, "end": v(-4349.3, 3.18) * mm});
            skLineSegment(sketch, "E32.2.0.0", {"start": v(-4342.94, 47.63) * mm, "end": v(-4336.6, 47.63) * mm});
            skLineSegment(sketch, "E32.2.0.1", {"start": v(-4336.6, 47.63) * mm, "end": v(-4336.6, 3.18) * mm});
            skLineSegment(sketch, "E32.2.0.2", {"start": v(-4342.94, 47.63) * mm, "end": v(-4342.94, 3.18) * mm});
            skLineSegment(sketch, "E32.2.0.3", {"start": v(-4342.94, 3.18) * mm, "end": v(-4336.6, 3.18) * mm});
            skLineSegment(sketch, "E32.3.0.0", {"start": v(-4330.24, 47.63) * mm, "end": v(-4323.9, 47.63) * mm});
            skLineSegment(sketch, "E32.3.0.1", {"start": v(-4323.9, 47.63) * mm, "end": v(-4323.9, 3.18) * mm});
            skLineSegment(sketch, "E32.3.0.2", {"start": v(-4330.24, 47.63) * mm, "end": v(-4330.24, 3.18) * mm});
            skLineSegment(sketch, "E32.3.0.3", {"start": v(-4330.24, 3.18) * mm, "end": v(-4323.9, 3.18) * mm});
            skLineSegment(sketch, "E32.4.0.0", {"start": v(-4317.54, 47.63) * mm, "end": v(-4311.2, 47.63) * mm});
            skLineSegment(sketch, "E32.4.0.1", {"start": v(-4311.2, 47.63) * mm, "end": v(-4311.2, 3.18) * mm});
            skLineSegment(sketch, "E32.4.0.2", {"start": v(-4317.54, 47.63) * mm, "end": v(-4317.54, 3.18) * mm});
            skLineSegment(sketch, "E32.4.0.3", {"start": v(-4317.54, 3.18) * mm, "end": v(-4311.2, 3.18) * mm});
            skLineSegment(sketch, "E32.5.0.0", {"start": v(-4304.84, 47.63) * mm, "end": v(-4298.5, 47.63) * mm});
            skLineSegment(sketch, "E32.5.0.1", {"start": v(-4298.5, 47.63) * mm, "end": v(-4298.5, 3.18) * mm});
            skLineSegment(sketch, "E32.5.0.2", {"start": v(-4304.84, 47.63) * mm, "end": v(-4304.84, 3.18) * mm});
            skLineSegment(sketch, "E32.5.0.3", {"start": v(-4304.84, 3.18) * mm, "end": v(-4298.5, 3.18) * mm});
            skLineSegment(sketch, "E32.6.0.0", {"start": v(-4292.14, 47.63) * mm, "end": v(-4285.8, 47.63) * mm});
            skLineSegment(sketch, "E32.6.0.1", {"start": v(-4285.8, 47.63) * mm, "end": v(-4285.8, 3.18) * mm});
            skLineSegment(sketch, "E32.6.0.2", {"start": v(-4292.14, 47.63) * mm, "end": v(-4292.14, 3.18) * mm});
            skLineSegment(sketch, "E32.6.0.3", {"start": v(-4292.14, 3.18) * mm, "end": v(-4285.8, 3.18) * mm});
            skLineSegment(sketch, "E32.7.0.0", {"start": v(-4279.44, 47.63) * mm, "end": v(-4273.1, 47.63) * mm});
            skLineSegment(sketch, "E32.7.0.1", {"start": v(-4273.1, 47.63) * mm, "end": v(-4273.1, 3.18) * mm});
            skLineSegment(sketch, "E32.7.0.2", {"start": v(-4279.44, 47.63) * mm, "end": v(-4279.44, 3.18) * mm});
            skLineSegment(sketch, "E32.7.0.3", {"start": v(-4279.44, 3.18) * mm, "end": v(-4273.1, 3.18) * mm});
            skLineSegment(sketch, "E32.8.0.0", {"start": v(-4266.74, 47.63) * mm, "end": v(-4260.4, 47.63) * mm});
            skLineSegment(sketch, "E32.8.0.1", {"start": v(-4260.4, 47.63) * mm, "end": v(-4260.4, 3.18) * mm});
            skLineSegment(sketch, "E32.8.0.2", {"start": v(-4266.74, 47.63) * mm, "end": v(-4266.74, 3.18) * mm});
            skLineSegment(sketch, "E32.8.0.3", {"start": v(-4266.74, 3.18) * mm, "end": v(-4260.4, 3.18) * mm});
            skLineSegment(sketch, "E32.9.0.0", {"start": v(-4254.04, 47.63) * mm, "end": v(-4247.7, 47.63) * mm});
            skLineSegment(sketch, "E32.9.0.1", {"start": v(-4247.7, 47.63) * mm, "end": v(-4247.7, 3.18) * mm});
            skLineSegment(sketch, "E32.9.0.2", {"start": v(-4254.04, 47.63) * mm, "end": v(-4254.04, 3.18) * mm});
            skLineSegment(sketch, "E32.9.0.3", {"start": v(-4254.04, 3.18) * mm, "end": v(-4247.7, 3.18) * mm});
            skLineSegment(sketch, "E32.10.0.0", {"start": v(-4241.34, 47.63) * mm, "end": v(-4235, 47.63) * mm});
            skLineSegment(sketch, "E32.10.0.1", {"start": v(-4235, 47.63) * mm, "end": v(-4235, 3.18) * mm});
            skLineSegment(sketch, "E32.10.0.2", {"start": v(-4241.34, 47.63) * mm, "end": v(-4241.34, 3.18) * mm});
            skLineSegment(sketch, "E32.10.0.3", {"start": v(-4241.34, 3.18) * mm, "end": v(-4235, 3.18) * mm});
            skLineSegment(sketch, "E32.11.0.0", {"start": v(-4228.64, 47.63) * mm, "end": v(-4222.3, 47.63) * mm});
            skLineSegment(sketch, "E32.11.0.1", {"start": v(-4222.3, 47.63) * mm, "end": v(-4222.3, 3.18) * mm});
            skLineSegment(sketch, "E32.11.0.2", {"start": v(-4228.64, 47.63) * mm, "end": v(-4228.64, 3.18) * mm});
            skLineSegment(sketch, "E32.11.0.3", {"start": v(-4228.64, 3.18) * mm, "end": v(-4222.3, 3.18) * mm});
            skLineSegment(sketch, "E32.12.0.0", {"start": v(-4215.94, 47.63) * mm, "end": v(-4209.6, 47.63) * mm});
            skLineSegment(sketch, "E32.12.0.1", {"start": v(-4209.6, 47.63) * mm, "end": v(-4209.6, 3.18) * mm});
            skLineSegment(sketch, "E32.12.0.2", {"start": v(-4215.94, 47.63) * mm, "end": v(-4215.94, 3.18) * mm});
            skLineSegment(sketch, "E32.12.0.3", {"start": v(-4215.94, 3.18) * mm, "end": v(-4209.6, 3.18) * mm});
            skLineSegment(sketch, "E32.13.0.0", {"start": v(-4203.24, 47.63) * mm, "end": v(-4196.9, 47.63) * mm});
            skLineSegment(sketch, "E32.13.0.1", {"start": v(-4196.9, 47.63) * mm, "end": v(-4196.9, 3.18) * mm});
            skLineSegment(sketch, "E32.13.0.2", {"start": v(-4203.24, 47.63) * mm, "end": v(-4203.24, 3.18) * mm});
            skLineSegment(sketch, "E32.13.0.3", {"start": v(-4203.24, 3.18) * mm, "end": v(-4196.9, 3.18) * mm});
            skLineSegment(sketch, "E32.14.0.0", {"start": v(-4190.54, 47.63) * mm, "end": v(-4184.2, 47.63) * mm});
            skLineSegment(sketch, "E32.14.0.1", {"start": v(-4184.2, 47.63) * mm, "end": v(-4184.2, 3.18) * mm});
            skLineSegment(sketch, "E32.14.0.2", {"start": v(-4190.54, 47.63) * mm, "end": v(-4190.54, 3.18) * mm});
            skLineSegment(sketch, "E32.14.0.3", {"start": v(-4190.54, 3.18) * mm, "end": v(-4184.2, 3.18) * mm});
            skLineSegment(sketch, "E32.15.0.0", {"start": v(-4177.84, 47.63) * mm, "end": v(-4171.5, 47.63) * mm});
            skLineSegment(sketch, "E32.15.0.1", {"start": v(-4171.5, 47.63) * mm, "end": v(-4171.5, 3.18) * mm});
            skLineSegment(sketch, "E32.15.0.2", {"start": v(-4177.84, 47.63) * mm, "end": v(-4177.84, 3.18) * mm});
            skLineSegment(sketch, "E32.15.0.3", {"start": v(-4177.84, 3.18) * mm, "end": v(-4171.5, 3.18) * mm});
            skLineSegment(sketch, "E32.16.0.0", {"start": v(-4165.14, 47.63) * mm, "end": v(-4158.8, 47.63) * mm});
            skLineSegment(sketch, "E32.16.0.1", {"start": v(-4158.8, 47.63) * mm, "end": v(-4158.8, 3.18) * mm});
            skLineSegment(sketch, "E32.16.0.2", {"start": v(-4165.14, 47.63) * mm, "end": v(-4165.14, 3.18) * mm});
            skLineSegment(sketch, "E32.16.0.3", {"start": v(-4165.14, 3.18) * mm, "end": v(-4158.8, 3.18) * mm});
            skLineSegment(sketch, "E32.17.0.0", {"start": v(-4152.44, 47.63) * mm, "end": v(-4146.1, 47.63) * mm});
            skLineSegment(sketch, "E32.17.0.1", {"start": v(-4146.1, 47.63) * mm, "end": v(-4146.1, 3.18) * mm});
            skLineSegment(sketch, "E32.17.0.2", {"start": v(-4152.44, 47.63) * mm, "end": v(-4152.44, 3.18) * mm});
            skLineSegment(sketch, "E32.17.0.3", {"start": v(-4152.44, 3.18) * mm, "end": v(-4146.1, 3.18) * mm});
            skLineSegment(sketch, "E32.18.0.0", {"start": v(-4139.74, 47.63) * mm, "end": v(-4133.4, 47.63) * mm});
            skLineSegment(sketch, "E32.18.0.1", {"start": v(-4133.4, 47.63) * mm, "end": v(-4133.4, 3.18) * mm});
            skLineSegment(sketch, "E32.18.0.2", {"start": v(-4139.74, 47.63) * mm, "end": v(-4139.74, 3.18) * mm});
            skLineSegment(sketch, "E32.18.0.3", {"start": v(-4139.74, 3.18) * mm, "end": v(-4133.4, 3.18) * mm});
            skLineSegment(sketch, "E32.19.0.0", {"start": v(-4127.04, 47.63) * mm, "end": v(-4120.7, 47.63) * mm});
            skLineSegment(sketch, "E32.19.0.1", {"start": v(-4120.7, 47.63) * mm, "end": v(-4120.7, 3.18) * mm});
            skLineSegment(sketch, "E32.19.0.2", {"start": v(-4127.04, 47.63) * mm, "end": v(-4127.04, 3.18) * mm});
            skLineSegment(sketch, "E32.19.0.3", {"start": v(-4127.04, 3.18) * mm, "end": v(-4120.7, 3.18) * mm});
            skLineSegment(sketch, "E32.20.0.0", {"start": v(-4114.34, 47.63) * mm, "end": v(-4108, 47.63) * mm});
            skLineSegment(sketch, "E32.20.0.1", {"start": v(-4108, 47.63) * mm, "end": v(-4108, 3.18) * mm});
            skLineSegment(sketch, "E32.20.0.2", {"start": v(-4114.34, 47.63) * mm, "end": v(-4114.34, 3.18) * mm});
            skLineSegment(sketch, "E32.20.0.3", {"start": v(-4114.34, 3.18) * mm, "end": v(-4108, 3.18) * mm});
            skLineSegment(sketch, "E32.21.0.0", {"start": v(-4101.64, 47.63) * mm, "end": v(-4095.3, 47.63) * mm});
            skLineSegment(sketch, "E32.21.0.1", {"start": v(-4095.3, 47.63) * mm, "end": v(-4095.3, 3.18) * mm});
            skLineSegment(sketch, "E32.21.0.2", {"start": v(-4101.64, 47.63) * mm, "end": v(-4101.64, 3.18) * mm});
            skLineSegment(sketch, "E32.21.0.3", {"start": v(-4101.64, 3.18) * mm, "end": v(-4095.3, 3.18) * mm});
            skLineSegment(sketch, "E32.22.0.0", {"start": v(-4088.94, 47.63) * mm, "end": v(-4082.6, 47.63) * mm});
            skLineSegment(sketch, "E32.22.0.1", {"start": v(-4082.6, 47.63) * mm, "end": v(-4082.6, 3.18) * mm});
            skLineSegment(sketch, "E32.22.0.2", {"start": v(-4088.94, 47.63) * mm, "end": v(-4088.94, 3.18) * mm});
            skLineSegment(sketch, "E32.22.0.3", {"start": v(-4088.94, 3.18) * mm, "end": v(-4082.6, 3.18) * mm});
            skLineSegment(sketch, "E32.23.0.0", {"start": v(-4076.24, 47.63) * mm, "end": v(-4069.9, 47.63) * mm});
            skLineSegment(sketch, "E32.23.0.1", {"start": v(-4069.9, 47.63) * mm, "end": v(-4069.9, 3.18) * mm});
            skLineSegment(sketch, "E32.23.0.2", {"start": v(-4076.24, 47.63) * mm, "end": v(-4076.24, 3.18) * mm});
            skLineSegment(sketch, "E32.23.0.3", {"start": v(-4076.24, 3.18) * mm, "end": v(-4069.9, 3.18) * mm});
            skLineSegment(sketch, "E32.24.0.0", {"start": v(-4063.54, 47.63) * mm, "end": v(-4057.2, 47.63) * mm});
            skLineSegment(sketch, "E32.24.0.1", {"start": v(-4057.2, 47.63) * mm, "end": v(-4057.2, 3.18) * mm});
            skLineSegment(sketch, "E32.24.0.2", {"start": v(-4063.54, 47.63) * mm, "end": v(-4063.54, 3.18) * mm});
            skLineSegment(sketch, "E32.24.0.3", {"start": v(-4063.54, 3.18) * mm, "end": v(-4057.2, 3.18) * mm});
            skLineSegment(sketch, "E32.25.0.0", {"start": v(-4050.84, 47.63) * mm, "end": v(-4044.5, 47.63) * mm});
            skLineSegment(sketch, "E32.25.0.1", {"start": v(-4044.5, 47.63) * mm, "end": v(-4044.5, 3.18) * mm});
            skLineSegment(sketch, "E32.25.0.2", {"start": v(-4050.84, 47.63) * mm, "end": v(-4050.84, 3.18) * mm});
            skLineSegment(sketch, "E32.25.0.3", {"start": v(-4050.84, 3.18) * mm, "end": v(-4044.5, 3.18) * mm});
            skLineSegment(sketch, "E32.26.0.0", {"start": v(-4038.14, 47.63) * mm, "end": v(-4031.8, 47.63) * mm});
            skLineSegment(sketch, "E32.26.0.1", {"start": v(-4031.8, 47.63) * mm, "end": v(-4031.8, 3.18) * mm});
            skLineSegment(sketch, "E32.26.0.2", {"start": v(-4038.14, 47.63) * mm, "end": v(-4038.14, 3.18) * mm});
            skLineSegment(sketch, "E32.26.0.3", {"start": v(-4038.14, 3.18) * mm, "end": v(-4031.8, 3.18) * mm});
            skLineSegment(sketch, "E32.27.0.0", {"start": v(-4025.44, 47.63) * mm, "end": v(-4019.1, 47.63) * mm});
            skLineSegment(sketch, "E32.27.0.1", {"start": v(-4019.1, 47.63) * mm, "end": v(-4019.1, 3.18) * mm});
            skLineSegment(sketch, "E32.27.0.2", {"start": v(-4025.44, 47.63) * mm, "end": v(-4025.44, 3.18) * mm});
            skLineSegment(sketch, "E32.27.0.3", {"start": v(-4025.44, 3.18) * mm, "end": v(-4019.1, 3.18) * mm});
            skLineSegment(sketch, "E32.28.0.0", {"start": v(-4012.74, 47.63) * mm, "end": v(-4006.4, 47.63) * mm});
            skLineSegment(sketch, "E32.28.0.1", {"start": v(-4006.4, 47.63) * mm, "end": v(-4006.4, 3.18) * mm});
            skLineSegment(sketch, "E32.28.0.2", {"start": v(-4012.74, 47.63) * mm, "end": v(-4012.74, 3.18) * mm});
            skLineSegment(sketch, "E32.28.0.3", {"start": v(-4012.74, 3.18) * mm, "end": v(-4006.4, 3.18) * mm});
            skLineSegment(sketch, "E32.29.0.0", {"start": v(-4000.04, 47.63) * mm, "end": v(-3993.7, 47.63) * mm});
            skLineSegment(sketch, "E32.29.0.1", {"start": v(-3993.7, 47.63) * mm, "end": v(-3993.7, 3.18) * mm});
            skLineSegment(sketch, "E32.29.0.2", {"start": v(-4000.04, 47.63) * mm, "end": v(-4000.04, 3.18) * mm});
            skLineSegment(sketch, "E32.29.0.3", {"start": v(-4000.04, 3.18) * mm, "end": v(-3993.7, 3.18) * mm});
            skLineSegment(sketch, "E32.30.0.0", {"start": v(-3987.34, 47.63) * mm, "end": v(-3981, 47.63) * mm});
            skLineSegment(sketch, "E32.30.0.1", {"start": v(-3981, 47.63) * mm, "end": v(-3981, 3.18) * mm});
            skLineSegment(sketch, "E32.30.0.2", {"start": v(-3987.34, 47.63) * mm, "end": v(-3987.34, 3.18) * mm});
            skLineSegment(sketch, "E32.30.0.3", {"start": v(-3987.34, 3.18) * mm, "end": v(-3981, 3.18) * mm});
            skLineSegment(sketch, "E32.31.0.0", {"start": v(-3974.64, 47.63) * mm, "end": v(-3968.3, 47.63) * mm});
            skLineSegment(sketch, "E32.31.0.1", {"start": v(-3968.3, 47.63) * mm, "end": v(-3968.3, 3.18) * mm});
            skLineSegment(sketch, "E32.31.0.2", {"start": v(-3974.64, 47.63) * mm, "end": v(-3974.64, 3.18) * mm});
            skLineSegment(sketch, "E32.31.0.3", {"start": v(-3974.64, 3.18) * mm, "end": v(-3968.3, 3.18) * mm});
            skLineSegment(sketch, "E32.32.0.0", {"start": v(-3961.94, 47.63) * mm, "end": v(-3955.6, 47.63) * mm});
            skLineSegment(sketch, "E32.32.0.1", {"start": v(-3955.6, 47.63) * mm, "end": v(-3955.6, 3.18) * mm});
            skLineSegment(sketch, "E32.32.0.2", {"start": v(-3961.94, 47.63) * mm, "end": v(-3961.94, 3.18) * mm});
            skLineSegment(sketch, "E32.32.0.3", {"start": v(-3961.94, 3.18) * mm, "end": v(-3955.6, 3.18) * mm});
            skLineSegment(sketch, "E32.33.0.0", {"start": v(-3949.24, 47.63) * mm, "end": v(-3942.9, 47.63) * mm});
            skLineSegment(sketch, "E32.33.0.1", {"start": v(-3942.9, 47.63) * mm, "end": v(-3942.9, 3.18) * mm});
            skLineSegment(sketch, "E32.33.0.2", {"start": v(-3949.24, 47.63) * mm, "end": v(-3949.24, 3.18) * mm});
            skLineSegment(sketch, "E32.33.0.3", {"start": v(-3949.24, 3.18) * mm, "end": v(-3942.9, 3.18) * mm});
            skLineSegment(sketch, "E32.34.0.0", {"start": v(-3936.54, 47.63) * mm, "end": v(-3930.2, 47.63) * mm});
            skLineSegment(sketch, "E32.34.0.1", {"start": v(-3930.2, 47.63) * mm, "end": v(-3930.2, 3.18) * mm});
            skLineSegment(sketch, "E32.34.0.2", {"start": v(-3936.54, 47.63) * mm, "end": v(-3936.54, 3.18) * mm});
            skLineSegment(sketch, "E32.34.0.3", {"start": v(-3936.54, 3.18) * mm, "end": v(-3930.2, 3.18) * mm});
            skLineSegment(sketch, "E32.35.0.0", {"start": v(-3923.84, 47.63) * mm, "end": v(-3917.5, 47.63) * mm});
            skLineSegment(sketch, "E32.35.0.1", {"start": v(-3917.5, 47.63) * mm, "end": v(-3917.5, 3.18) * mm});
            skLineSegment(sketch, "E32.35.0.2", {"start": v(-3923.84, 47.63) * mm, "end": v(-3923.84, 3.18) * mm});
            skLineSegment(sketch, "E32.35.0.3", {"start": v(-3923.84, 3.18) * mm, "end": v(-3917.5, 3.18) * mm});
            skLineSegment(sketch, "E32.36.0.0", {"start": v(-3911.14, 47.63) * mm, "end": v(-3904.8, 47.63) * mm});
            skLineSegment(sketch, "E32.36.0.1", {"start": v(-3904.8, 47.63) * mm, "end": v(-3904.8, 3.18) * mm});
            skLineSegment(sketch, "E32.36.0.2", {"start": v(-3911.14, 47.63) * mm, "end": v(-3911.14, 3.18) * mm});
            skLineSegment(sketch, "E32.36.0.3", {"start": v(-3911.14, 3.18) * mm, "end": v(-3904.8, 3.18) * mm});
            skLineSegment(sketch, "E32.37.0.0", {"start": v(-3898.44, 47.63) * mm, "end": v(-3892.1, 47.63) * mm});
            skLineSegment(sketch, "E32.37.0.1", {"start": v(-3892.1, 47.63) * mm, "end": v(-3892.1, 3.18) * mm});
            skLineSegment(sketch, "E32.37.0.2", {"start": v(-3898.44, 47.63) * mm, "end": v(-3898.44, 3.18) * mm});
            skLineSegment(sketch, "E32.37.0.3", {"start": v(-3898.44, 3.18) * mm, "end": v(-3892.1, 3.18) * mm});
            skLineSegment(sketch, "E32.38.0.0", {"start": v(-3885.74, 47.63) * mm, "end": v(-3879.4, 47.63) * mm});
            skLineSegment(sketch, "E32.38.0.1", {"start": v(-3879.4, 47.63) * mm, "end": v(-3879.4, 3.18) * mm});
            skLineSegment(sketch, "E32.38.0.2", {"start": v(-3885.74, 47.63) * mm, "end": v(-3885.74, 3.18) * mm});
            skLineSegment(sketch, "E32.38.0.3", {"start": v(-3885.74, 3.18) * mm, "end": v(-3879.4, 3.18) * mm});
            skLineSegment(sketch, "E32.39.0.0", {"start": v(-3873.04, 47.63) * mm, "end": v(-3866.7, 47.63) * mm});
            skLineSegment(sketch, "E32.39.0.1", {"start": v(-3866.7, 47.63) * mm, "end": v(-3866.7, 3.18) * mm});
            skLineSegment(sketch, "E32.39.0.2", {"start": v(-3873.04, 47.63) * mm, "end": v(-3873.04, 3.18) * mm});
            skLineSegment(sketch, "E32.39.0.3", {"start": v(-3873.04, 3.18) * mm, "end": v(-3866.7, 3.18) * mm});
            skLineSegment(sketch, "E32.40.0.0", {"start": v(-3860.34, 47.63) * mm, "end": v(-3854, 47.63) * mm});
            skLineSegment(sketch, "E32.40.0.1", {"start": v(-3854, 47.63) * mm, "end": v(-3854, 3.18) * mm});
            skLineSegment(sketch, "E32.40.0.2", {"start": v(-3860.34, 47.63) * mm, "end": v(-3860.34, 3.18) * mm});
            skLineSegment(sketch, "E32.40.0.3", {"start": v(-3860.34, 3.18) * mm, "end": v(-3854, 3.18) * mm});
            skLineSegment(sketch, "E32.41.0.0", {"start": v(-3847.64, 47.63) * mm, "end": v(-3841.3, 47.63) * mm});
            skLineSegment(sketch, "E32.41.0.1", {"start": v(-3841.3, 47.63) * mm, "end": v(-3841.3, 3.18) * mm});
            skLineSegment(sketch, "E32.41.0.2", {"start": v(-3847.64, 47.63) * mm, "end": v(-3847.64, 3.18) * mm});
            skLineSegment(sketch, "E32.41.0.3", {"start": v(-3847.64, 3.18) * mm, "end": v(-3841.3, 3.18) * mm});
            skLineSegment(sketch, "E32.42.0.0", {"start": v(-3834.94, 47.63) * mm, "end": v(-3828.6, 47.63) * mm});
            skLineSegment(sketch, "E32.42.0.1", {"start": v(-3828.6, 47.63) * mm, "end": v(-3828.6, 3.18) * mm});
            skLineSegment(sketch, "E32.42.0.2", {"start": v(-3834.94, 47.63) * mm, "end": v(-3834.94, 3.18) * mm});
            skLineSegment(sketch, "E32.42.0.3", {"start": v(-3834.94, 3.18) * mm, "end": v(-3828.6, 3.18) * mm});
            skLineSegment(sketch, "E32.43.0.0", {"start": v(-3822.24, 47.63) * mm, "end": v(-3815.9, 47.63) * mm});
            skLineSegment(sketch, "E32.43.0.1", {"start": v(-3815.9, 47.63) * mm, "end": v(-3815.9, 3.18) * mm});
            skLineSegment(sketch, "E32.43.0.2", {"start": v(-3822.24, 47.63) * mm, "end": v(-3822.24, 3.18) * mm});
            skLineSegment(sketch, "E32.43.0.3", {"start": v(-3822.24, 3.18) * mm, "end": v(-3815.9, 3.18) * mm});
            skLineSegment(sketch, "E32.44.0.0", {"start": v(-3809.54, 47.63) * mm, "end": v(-3803.2, 47.63) * mm});
            skLineSegment(sketch, "E32.44.0.1", {"start": v(-3803.2, 47.63) * mm, "end": v(-3803.2, 3.18) * mm});
            skLineSegment(sketch, "E32.44.0.2", {"start": v(-3809.54, 47.63) * mm, "end": v(-3809.54, 3.18) * mm});
            skLineSegment(sketch, "E32.44.0.3", {"start": v(-3809.54, 3.18) * mm, "end": v(-3803.2, 3.18) * mm});
            skLineSegment(sketch, "E32.45.0.0", {"start": v(-3796.84, 47.63) * mm, "end": v(-3790.5, 47.63) * mm});
            skLineSegment(sketch, "E32.45.0.1", {"start": v(-3790.5, 47.63) * mm, "end": v(-3790.5, 3.18) * mm});
            skLineSegment(sketch, "E32.45.0.2", {"start": v(-3796.84, 47.63) * mm, "end": v(-3796.84, 3.18) * mm});
            skLineSegment(sketch, "E32.45.0.3", {"start": v(-3796.84, 3.18) * mm, "end": v(-3790.5, 3.18) * mm});
            skLineSegment(sketch, "E32.46.0.0", {"start": v(-3784.14, 47.63) * mm, "end": v(-3777.8, 47.63) * mm});
            skLineSegment(sketch, "E32.46.0.1", {"start": v(-3777.8, 47.63) * mm, "end": v(-3777.8, 3.18) * mm});
            skLineSegment(sketch, "E32.46.0.2", {"start": v(-3784.14, 47.63) * mm, "end": v(-3784.14, 3.18) * mm});
            skLineSegment(sketch, "E32.46.0.3", {"start": v(-3784.14, 3.18) * mm, "end": v(-3777.8, 3.18) * mm});
            skLineSegment(sketch, "E32.47.0.0", {"start": v(-3771.44, 47.63) * mm, "end": v(-3765.1, 47.63) * mm});
            skLineSegment(sketch, "E32.47.0.1", {"start": v(-3765.1, 47.63) * mm, "end": v(-3765.1, 3.18) * mm});
            skLineSegment(sketch, "E32.47.0.2", {"start": v(-3771.44, 47.63) * mm, "end": v(-3771.44, 3.18) * mm});
            skLineSegment(sketch, "E32.47.0.3", {"start": v(-3771.44, 3.18) * mm, "end": v(-3765.1, 3.18) * mm});
            skLineSegment(sketch, "E32.48.0.0", {"start": v(-3758.74, 47.63) * mm, "end": v(-3752.4, 47.63) * mm});
            skLineSegment(sketch, "E32.48.0.1", {"start": v(-3752.4, 47.63) * mm, "end": v(-3752.4, 3.18) * mm});
            skLineSegment(sketch, "E32.48.0.2", {"start": v(-3758.74, 47.63) * mm, "end": v(-3758.74, 3.18) * mm});
            skLineSegment(sketch, "E32.48.0.3", {"start": v(-3758.74, 3.18) * mm, "end": v(-3752.4, 3.18) * mm});
            skLineSegment(sketch, "E32.49.0.0", {"start": v(-3746.04, 47.63) * mm, "end": v(-3739.7, 47.63) * mm});
            skLineSegment(sketch, "E32.49.0.1", {"start": v(-3739.7, 47.63) * mm, "end": v(-3739.7, 3.18) * mm});
            skLineSegment(sketch, "E32.49.0.2", {"start": v(-3746.04, 47.63) * mm, "end": v(-3746.04, 3.18) * mm});
            skLineSegment(sketch, "E32.49.0.3", {"start": v(-3746.04, 3.18) * mm, "end": v(-3739.7, 3.18) * mm});
            skLineSegment(sketch, "E32.50.0.0", {"start": v(-3733.34, 47.63) * mm, "end": v(-3727, 47.63) * mm});
            skLineSegment(sketch, "E32.50.0.1", {"start": v(-3727, 47.63) * mm, "end": v(-3727, 3.18) * mm});
            skLineSegment(sketch, "E32.50.0.2", {"start": v(-3733.34, 47.63) * mm, "end": v(-3733.34, 3.18) * mm});
            skLineSegment(sketch, "E32.50.0.3", {"start": v(-3733.34, 3.18) * mm, "end": v(-3727, 3.18) * mm});
            skLineSegment(sketch, "E32.51.0.0", {"start": v(-3720.64, 47.63) * mm, "end": v(-3714.3, 47.63) * mm});
            skLineSegment(sketch, "E32.51.0.1", {"start": v(-3714.3, 47.63) * mm, "end": v(-3714.3, 3.18) * mm});
            skLineSegment(sketch, "E32.51.0.2", {"start": v(-3720.64, 47.63) * mm, "end": v(-3720.64, 3.18) * mm});
            skLineSegment(sketch, "E32.51.0.3", {"start": v(-3720.64, 3.18) * mm, "end": v(-3714.3, 3.18) * mm});
            skLineSegment(sketch, "E32.52.0.0", {"start": v(-3707.94, 47.63) * mm, "end": v(-3701.6, 47.63) * mm});
            skLineSegment(sketch, "E32.52.0.1", {"start": v(-3701.6, 47.63) * mm, "end": v(-3701.6, 3.18) * mm});
            skLineSegment(sketch, "E32.52.0.2", {"start": v(-3707.94, 47.63) * mm, "end": v(-3707.94, 3.18) * mm});
            skLineSegment(sketch, "E32.52.0.3", {"start": v(-3707.94, 3.18) * mm, "end": v(-3701.6, 3.18) * mm});
            skLineSegment(sketch, "E32.53.0.0", {"start": v(-3695.24, 47.63) * mm, "end": v(-3688.9, 47.63) * mm});
            skLineSegment(sketch, "E32.53.0.1", {"start": v(-3688.9, 47.63) * mm, "end": v(-3688.9, 3.18) * mm});
            skLineSegment(sketch, "E32.53.0.2", {"start": v(-3695.24, 47.63) * mm, "end": v(-3695.24, 3.18) * mm});
            skLineSegment(sketch, "E32.53.0.3", {"start": v(-3695.24, 3.18) * mm, "end": v(-3688.9, 3.18) * mm});
            skLineSegment(sketch, "E32.54.0.0", {"start": v(-3682.54, 47.63) * mm, "end": v(-3676.2, 47.63) * mm});
            skLineSegment(sketch, "E32.54.0.1", {"start": v(-3676.2, 47.63) * mm, "end": v(-3676.2, 3.18) * mm});
            skLineSegment(sketch, "E32.54.0.2", {"start": v(-3682.54, 47.63) * mm, "end": v(-3682.54, 3.18) * mm});
            skLineSegment(sketch, "E32.54.0.3", {"start": v(-3682.54, 3.18) * mm, "end": v(-3676.2, 3.18) * mm});
            skLineSegment(sketch, "E32.55.0.0", {"start": v(-3669.84, 47.63) * mm, "end": v(-3663.5, 47.63) * mm});
            skLineSegment(sketch, "E32.55.0.1", {"start": v(-3663.5, 47.63) * mm, "end": v(-3663.5, 3.18) * mm});
            skLineSegment(sketch, "E32.55.0.2", {"start": v(-3669.84, 47.63) * mm, "end": v(-3669.84, 3.18) * mm});
            skLineSegment(sketch, "E32.55.0.3", {"start": v(-3669.84, 3.18) * mm, "end": v(-3663.5, 3.18) * mm});
            skLineSegment(sketch, "E32.56.0.0", {"start": v(-3657.14, 47.63) * mm, "end": v(-3650.8, 47.63) * mm});
            skLineSegment(sketch, "E32.56.0.1", {"start": v(-3650.8, 47.63) * mm, "end": v(-3650.8, 3.18) * mm});
            skLineSegment(sketch, "E32.56.0.2", {"start": v(-3657.14, 47.63) * mm, "end": v(-3657.14, 3.18) * mm});
            skLineSegment(sketch, "E32.56.0.3", {"start": v(-3657.14, 3.18) * mm, "end": v(-3650.8, 3.18) * mm});
            skLineSegment(sketch, "E32.57.0.0", {"start": v(-3644.44, 47.63) * mm, "end": v(-3638.1, 47.63) * mm});
            skLineSegment(sketch, "E32.57.0.1", {"start": v(-3638.1, 47.63) * mm, "end": v(-3638.1, 3.18) * mm});
            skLineSegment(sketch, "E32.57.0.2", {"start": v(-3644.44, 47.63) * mm, "end": v(-3644.44, 3.18) * mm});
            skLineSegment(sketch, "E32.57.0.3", {"start": v(-3644.44, 3.18) * mm, "end": v(-3638.1, 3.18) * mm});
            skLineSegment(sketch, "E32.58.0.0", {"start": v(-3631.74, 47.63) * mm, "end": v(-3625.4, 47.63) * mm});
            skLineSegment(sketch, "E32.58.0.1", {"start": v(-3625.4, 47.63) * mm, "end": v(-3625.4, 3.18) * mm});
            skLineSegment(sketch, "E32.58.0.2", {"start": v(-3631.74, 47.63) * mm, "end": v(-3631.74, 3.18) * mm});
            skLineSegment(sketch, "E32.58.0.3", {"start": v(-3631.74, 3.18) * mm, "end": v(-3625.4, 3.18) * mm});
            skLineSegment(sketch, "E32.59.0.0", {"start": v(-3619.04, 47.63) * mm, "end": v(-3612.7, 47.63) * mm});
            skLineSegment(sketch, "E32.59.0.1", {"start": v(-3612.7, 47.63) * mm, "end": v(-3612.7, 3.18) * mm});
            skLineSegment(sketch, "E32.59.0.2", {"start": v(-3619.04, 47.63) * mm, "end": v(-3619.04, 3.18) * mm});
            skLineSegment(sketch, "E32.59.0.3", {"start": v(-3619.04, 3.18) * mm, "end": v(-3612.7, 3.18) * mm});
            skLineSegment(sketch, "E32.direction1", {"start": v(-4368.34, 47.63) * mm, "end": v(-4355.64, 47.63) * mm, "construction": true});
            skSolve(sketch);
        }
        {
            var Q0;
            Q0=makeQuery(id+"F20.imprint","IMPRINT",FACE,{"disambiguationData":[TD([[makeQuery(id+"F20.imprint","IMPRINT",EDGE,{"derivedFrom":sQuery(id+"F20.wireOp",EDGE,"E31.bottom")}),-1.0]])]});
            var Q1;
            Q1=makeQuery(id+"F20.imprint","IMPRINT",FACE,{"disambiguationData":[TD([[makeQuery(id+"F20.imprint","IMPRINT",EDGE,{"derivedFrom":sQuery(id+"F20.wireOp",EDGE,"E32.1.0.0")}),-1.0]])]});
            var Q2;
            Q2=makeQuery(id+"F20.imprint","IMPRINT",FACE,{"disambiguationData":[TD([[makeQuery(id+"F20.imprint","IMPRINT",EDGE,{"derivedFrom":sQuery(id+"F20.wireOp",EDGE,"E32.2.0.0")}),-1.0]])]});
            var Q3;
            Q3=makeQuery(id+"F20.imprint","IMPRINT",FACE,{"disambiguationData":[TD([[makeQuery(id+"F20.imprint","IMPRINT",EDGE,{"derivedFrom":sQuery(id+"F20.wireOp",EDGE,"E32.3.0.0")}),-1.0]])]});
            var Q4;
            Q4=makeQuery(id+"F20.imprint","IMPRINT",FACE,{"disambiguationData":[TD([[makeQuery(id+"F20.imprint","IMPRINT",EDGE,{"derivedFrom":sQuery(id+"F20.wireOp",EDGE,"E32.4.0.0")}),-1.0]])]});
            var Q5;
            Q5=makeQuery(id+"F20.imprint","IMPRINT",FACE,{"disambiguationData":[TD([[makeQuery(id+"F20.imprint","IMPRINT",EDGE,{"derivedFrom":sQuery(id+"F20.wireOp",EDGE,"E32.5.0.0")}),-1.0]])]});
            var Q6;
            Q6=makeQuery(id+"F20.imprint","IMPRINT",FACE,{"disambiguationData":[TD([[makeQuery(id+"F20.imprint","IMPRINT",EDGE,{"derivedFrom":sQuery(id+"F20.wireOp",EDGE,"E32.6.0.0")}),-1.0]])]});
            var Q7;
            Q7=makeQuery(id+"F20.imprint","IMPRINT",FACE,{"disambiguationData":[TD([[makeQuery(id+"F20.imprint","IMPRINT",EDGE,{"derivedFrom":sQuery(id+"F20.wireOp",EDGE,"E32.7.0.0")}),-1.0]])]});
            var Q8;
            Q8=makeQuery(id+"F20.imprint","IMPRINT",FACE,{"disambiguationData":[TD([[makeQuery(id+"F20.imprint","IMPRINT",EDGE,{"derivedFrom":sQuery(id+"F20.wireOp",EDGE,"E32.8.0.0")}),-1.0]])]});
            var Q9;
            Q9=makeQuery(id+"F20.imprint","IMPRINT",FACE,{"disambiguationData":[TD([[makeQuery(id+"F20.imprint","IMPRINT",EDGE,{"derivedFrom":sQuery(id+"F20.wireOp",EDGE,"E32.9.0.0")}),-1.0]])]});
            var Q10;
            Q10=makeQuery(id+"F20.imprint","IMPRINT",FACE,{"disambiguationData":[TD([[makeQuery(id+"F20.imprint","IMPRINT",EDGE,{"derivedFrom":sQuery(id+"F20.wireOp",EDGE,"E32.10.0.0")}),-1.0]])]});
            var Q11;
            Q11=makeQuery(id+"F20.imprint","IMPRINT",FACE,{"disambiguationData":[TD([[makeQuery(id+"F20.imprint","IMPRINT",EDGE,{"derivedFrom":sQuery(id+"F20.wireOp",EDGE,"E32.11.0.0")}),-1.0]])]});
            var Q12;
            Q12=makeQuery(id+"F20.imprint","IMPRINT",FACE,{"disambiguationData":[TD([[makeQuery(id+"F20.imprint","IMPRINT",EDGE,{"derivedFrom":sQuery(id+"F20.wireOp",EDGE,"E32.12.0.0")}),-1.0]])]});
            var Q13;
            Q13=makeQuery(id+"F20.imprint","IMPRINT",FACE,{"disambiguationData":[TD([[makeQuery(id+"F20.imprint","IMPRINT",EDGE,{"derivedFrom":sQuery(id+"F20.wireOp",EDGE,"E32.13.0.0")}),-1.0]])]});
            var Q14;
            Q14=makeQuery(id+"F20.imprint","IMPRINT",FACE,{"disambiguationData":[TD([[makeQuery(id+"F20.imprint","IMPRINT",EDGE,{"derivedFrom":sQuery(id+"F20.wireOp",EDGE,"E32.14.0.0")}),-1.0]])]});
            var Q15;
            Q15=makeQuery(id+"F20.imprint","IMPRINT",FACE,{"disambiguationData":[TD([[makeQuery(id+"F20.imprint","IMPRINT",EDGE,{"derivedFrom":sQuery(id+"F20.wireOp",EDGE,"E32.15.0.0")}),-1.0]])]});
            var Q16;
            Q16=makeQuery(id+"F20.imprint","IMPRINT",FACE,{"disambiguationData":[TD([[makeQuery(id+"F20.imprint","IMPRINT",EDGE,{"derivedFrom":sQuery(id+"F20.wireOp",EDGE,"E32.16.0.0")}),-1.0]])]});
            var Q17;
            Q17=makeQuery(id+"F20.imprint","IMPRINT",FACE,{"disambiguationData":[TD([[makeQuery(id+"F20.imprint","IMPRINT",EDGE,{"derivedFrom":sQuery(id+"F20.wireOp",EDGE,"E32.17.0.0")}),-1.0]])]});
            var Q18;
            Q18=makeQuery(id+"F20.imprint","IMPRINT",FACE,{"disambiguationData":[TD([[makeQuery(id+"F20.imprint","IMPRINT",EDGE,{"derivedFrom":sQuery(id+"F20.wireOp",EDGE,"E32.18.0.0")}),-1.0]])]});
            var Q19;
            Q19=makeQuery(id+"F20.imprint","IMPRINT",FACE,{"disambiguationData":[TD([[makeQuery(id+"F20.imprint","IMPRINT",EDGE,{"derivedFrom":sQuery(id+"F20.wireOp",EDGE,"E32.19.0.0")}),-1.0]])]});
            var Q20;
            Q20=makeQuery(id+"F20.imprint","IMPRINT",FACE,{"disambiguationData":[TD([[makeQuery(id+"F20.imprint","IMPRINT",EDGE,{"derivedFrom":sQuery(id+"F20.wireOp",EDGE,"E32.20.0.0")}),-1.0]])]});
            var Q21;
            Q21=makeQuery(id+"F20.imprint","IMPRINT",FACE,{"disambiguationData":[TD([[makeQuery(id+"F20.imprint","IMPRINT",EDGE,{"derivedFrom":sQuery(id+"F20.wireOp",EDGE,"E32.21.0.0")}),-1.0]])]});
            var Q22;
            Q22=makeQuery(id+"F20.imprint","IMPRINT",FACE,{"disambiguationData":[TD([[makeQuery(id+"F20.imprint","IMPRINT",EDGE,{"derivedFrom":sQuery(id+"F20.wireOp",EDGE,"E32.22.0.0")}),-1.0]])]});
            var Q23;
            Q23=makeQuery(id+"F20.imprint","IMPRINT",FACE,{"disambiguationData":[TD([[makeQuery(id+"F20.imprint","IMPRINT",EDGE,{"derivedFrom":sQuery(id+"F20.wireOp",EDGE,"E32.23.0.0")}),-1.0]])]});
            var Q24;
            Q24=makeQuery(id+"F20.imprint","IMPRINT",FACE,{"disambiguationData":[TD([[makeQuery(id+"F20.imprint","IMPRINT",EDGE,{"derivedFrom":sQuery(id+"F20.wireOp",EDGE,"E32.24.0.0")}),-1.0]])]});
            var Q25;
            Q25=makeQuery(id+"F20.imprint","IMPRINT",FACE,{"disambiguationData":[TD([[makeQuery(id+"F20.imprint","IMPRINT",EDGE,{"derivedFrom":sQuery(id+"F20.wireOp",EDGE,"E32.25.0.0")}),-1.0]])]});
            var Q26;
            Q26=makeQuery(id+"F20.imprint","IMPRINT",FACE,{"disambiguationData":[TD([[makeQuery(id+"F20.imprint","IMPRINT",EDGE,{"derivedFrom":sQuery(id+"F20.wireOp",EDGE,"E32.26.0.0")}),-1.0]])]});
            var Q27;
            Q27=makeQuery(id+"F20.imprint","IMPRINT",FACE,{"disambiguationData":[TD([[makeQuery(id+"F20.imprint","IMPRINT",EDGE,{"derivedFrom":sQuery(id+"F20.wireOp",EDGE,"E32.27.0.0")}),-1.0]])]});
            var Q28;
            Q28=makeQuery(id+"F20.imprint","IMPRINT",FACE,{"disambiguationData":[TD([[makeQuery(id+"F20.imprint","IMPRINT",EDGE,{"derivedFrom":sQuery(id+"F20.wireOp",EDGE,"E32.28.0.0")}),-1.0]])]});
            var Q29;
            Q29=makeQuery(id+"F20.imprint","IMPRINT",FACE,{"disambiguationData":[TD([[makeQuery(id+"F20.imprint","IMPRINT",EDGE,{"derivedFrom":sQuery(id+"F20.wireOp",EDGE,"E32.29.0.0")}),-1.0]])]});
            var Q30;
            Q30=makeQuery(id+"F20.imprint","IMPRINT",FACE,{"disambiguationData":[TD([[makeQuery(id+"F20.imprint","IMPRINT",EDGE,{"derivedFrom":sQuery(id+"F20.wireOp",EDGE,"E32.30.0.0")}),-1.0]])]});
            var Q31;
            Q31=makeQuery(id+"F20.imprint","IMPRINT",FACE,{"disambiguationData":[TD([[makeQuery(id+"F20.imprint","IMPRINT",EDGE,{"derivedFrom":sQuery(id+"F20.wireOp",EDGE,"E32.31.0.0")}),-1.0]])]});
            var Q32;
            Q32=makeQuery(id+"F20.imprint","IMPRINT",FACE,{"disambiguationData":[TD([[makeQuery(id+"F20.imprint","IMPRINT",EDGE,{"derivedFrom":sQuery(id+"F20.wireOp",EDGE,"E32.32.0.0")}),-1.0]])]});
            var Q33;
            Q33=makeQuery(id+"F20.imprint","IMPRINT",FACE,{"disambiguationData":[TD([[makeQuery(id+"F20.imprint","IMPRINT",EDGE,{"derivedFrom":sQuery(id+"F20.wireOp",EDGE,"E32.33.0.0")}),-1.0]])]});
            var Q34;
            Q34=makeQuery(id+"F20.imprint","IMPRINT",FACE,{"disambiguationData":[TD([[makeQuery(id+"F20.imprint","IMPRINT",EDGE,{"derivedFrom":sQuery(id+"F20.wireOp",EDGE,"E32.34.0.0")}),-1.0]])]});
            var Q35;
            Q35=makeQuery(id+"F20.imprint","IMPRINT",FACE,{"disambiguationData":[TD([[makeQuery(id+"F20.imprint","IMPRINT",EDGE,{"derivedFrom":sQuery(id+"F20.wireOp",EDGE,"E32.35.0.0")}),-1.0]])]});
            var Q36;
            Q36=makeQuery(id+"F20.imprint","IMPRINT",FACE,{"disambiguationData":[TD([[makeQuery(id+"F20.imprint","IMPRINT",EDGE,{"derivedFrom":sQuery(id+"F20.wireOp",EDGE,"E32.36.0.0")}),-1.0]])]});
            var Q37;
            Q37=makeQuery(id+"F20.imprint","IMPRINT",FACE,{"disambiguationData":[TD([[makeQuery(id+"F20.imprint","IMPRINT",EDGE,{"derivedFrom":sQuery(id+"F20.wireOp",EDGE,"E32.37.0.0")}),-1.0]])]});
            var Q38;
            Q38=makeQuery(id+"F20.imprint","IMPRINT",FACE,{"disambiguationData":[TD([[makeQuery(id+"F20.imprint","IMPRINT",EDGE,{"derivedFrom":sQuery(id+"F20.wireOp",EDGE,"E32.38.0.0")}),-1.0]])]});
            var Q39;
            Q39=makeQuery(id+"F20.imprint","IMPRINT",FACE,{"disambiguationData":[TD([[makeQuery(id+"F20.imprint","IMPRINT",EDGE,{"derivedFrom":sQuery(id+"F20.wireOp",EDGE,"E32.39.0.0")}),-1.0]])]});
            var Q40;
            Q40=makeQuery(id+"F20.imprint","IMPRINT",FACE,{"disambiguationData":[TD([[makeQuery(id+"F20.imprint","IMPRINT",EDGE,{"derivedFrom":sQuery(id+"F20.wireOp",EDGE,"E32.40.0.0")}),-1.0]])]});
            var Q41;
            Q41=makeQuery(id+"F20.imprint","IMPRINT",FACE,{"disambiguationData":[TD([[makeQuery(id+"F20.imprint","IMPRINT",EDGE,{"derivedFrom":sQuery(id+"F20.wireOp",EDGE,"E32.41.0.0")}),-1.0]])]});
            var Q42;
            Q42=makeQuery(id+"F20.imprint","IMPRINT",FACE,{"disambiguationData":[TD([[makeQuery(id+"F20.imprint","IMPRINT",EDGE,{"derivedFrom":sQuery(id+"F20.wireOp",EDGE,"E32.42.0.0")}),-1.0]])]});
            var Q43;
            Q43=makeQuery(id+"F20.imprint","IMPRINT",FACE,{"disambiguationData":[TD([[makeQuery(id+"F20.imprint","IMPRINT",EDGE,{"derivedFrom":sQuery(id+"F20.wireOp",EDGE,"E32.43.0.0")}),-1.0]])]});
            var Q44;
            Q44=makeQuery(id+"F20.imprint","IMPRINT",FACE,{"disambiguationData":[TD([[makeQuery(id+"F20.imprint","IMPRINT",EDGE,{"derivedFrom":sQuery(id+"F20.wireOp",EDGE,"E32.44.0.0")}),-1.0]])]});
            var Q45;
            Q45=makeQuery(id+"F20.imprint","IMPRINT",FACE,{"disambiguationData":[TD([[makeQuery(id+"F20.imprint","IMPRINT",EDGE,{"derivedFrom":sQuery(id+"F20.wireOp",EDGE,"E32.45.0.0")}),-1.0]])]});
            var Q46;
            Q46=makeQuery(id+"F20.imprint","IMPRINT",FACE,{"disambiguationData":[TD([[makeQuery(id+"F20.imprint","IMPRINT",EDGE,{"derivedFrom":sQuery(id+"F20.wireOp",EDGE,"E32.46.0.0")}),-1.0]])]});
            var Q47;
            Q47=makeQuery(id+"F20.imprint","IMPRINT",FACE,{"disambiguationData":[TD([[makeQuery(id+"F20.imprint","IMPRINT",EDGE,{"derivedFrom":sQuery(id+"F20.wireOp",EDGE,"E32.47.0.0")}),-1.0]])]});
            var Q48;
            Q48=makeQuery(id+"F20.imprint","IMPRINT",FACE,{"disambiguationData":[TD([[makeQuery(id+"F20.imprint","IMPRINT",EDGE,{"derivedFrom":sQuery(id+"F20.wireOp",EDGE,"E32.48.0.0")}),-1.0]])]});
            var Q49;
            Q49=makeQuery(id+"F20.imprint","IMPRINT",FACE,{"disambiguationData":[TD([[makeQuery(id+"F20.imprint","IMPRINT",EDGE,{"derivedFrom":sQuery(id+"F20.wireOp",EDGE,"E32.49.0.0")}),-1.0]])]});
            var Q50;
            Q50=makeQuery(id+"F20.imprint","IMPRINT",FACE,{"disambiguationData":[TD([[makeQuery(id+"F20.imprint","IMPRINT",EDGE,{"derivedFrom":sQuery(id+"F20.wireOp",EDGE,"E32.50.0.0")}),-1.0]])]});
            var Q51;
            Q51=makeQuery(id+"F20.imprint","IMPRINT",FACE,{"disambiguationData":[TD([[makeQuery(id+"F20.imprint","IMPRINT",EDGE,{"derivedFrom":sQuery(id+"F20.wireOp",EDGE,"E32.51.0.0")}),-1.0]])]});
            var Q52;
            Q52=makeQuery(id+"F20.imprint","IMPRINT",FACE,{"disambiguationData":[TD([[makeQuery(id+"F20.imprint","IMPRINT",EDGE,{"derivedFrom":sQuery(id+"F20.wireOp",EDGE,"E32.52.0.0")}),-1.0]])]});
            var Q53;
            Q53=makeQuery(id+"F20.imprint","IMPRINT",FACE,{"disambiguationData":[TD([[makeQuery(id+"F20.imprint","IMPRINT",EDGE,{"derivedFrom":sQuery(id+"F20.wireOp",EDGE,"E32.53.0.0")}),-1.0]])]});
            var Q54;
            Q54=makeQuery(id+"F20.imprint","IMPRINT",FACE,{"disambiguationData":[TD([[makeQuery(id+"F20.imprint","IMPRINT",EDGE,{"derivedFrom":sQuery(id+"F20.wireOp",EDGE,"E32.54.0.0")}),-1.0]])]});
            var Q55;
            Q55=makeQuery(id+"F20.imprint","IMPRINT",FACE,{"disambiguationData":[TD([[makeQuery(id+"F20.imprint","IMPRINT",EDGE,{"derivedFrom":sQuery(id+"F20.wireOp",EDGE,"E32.55.0.0")}),-1.0]])]});
            var Q56;
            Q56=makeQuery(id+"F20.imprint","IMPRINT",FACE,{"disambiguationData":[TD([[makeQuery(id+"F20.imprint","IMPRINT",EDGE,{"derivedFrom":sQuery(id+"F20.wireOp",EDGE,"E32.56.0.0")}),-1.0]])]});
            var Q57;
            Q57=makeQuery(id+"F20.imprint","IMPRINT",FACE,{"disambiguationData":[TD([[makeQuery(id+"F20.imprint","IMPRINT",EDGE,{"derivedFrom":sQuery(id+"F20.wireOp",EDGE,"E32.57.0.0")}),-1.0]])]});
            var Q58;
            Q58=makeQuery(id+"F20.imprint","IMPRINT",FACE,{"disambiguationData":[TD([[makeQuery(id+"F20.imprint","IMPRINT",EDGE,{"derivedFrom":sQuery(id+"F20.wireOp",EDGE,"E32.58.0.0")}),-1.0]])]});
            extrude(context, id + "F21", {"entities" : qUnion([Q0, Q1, Q2, Q3, Q4, Q5, Q6, Q7, Q8, Q9, Q10, Q11, Q12, Q13, Q14, Q15, Q16, Q17, Q18, Q19, Q20, Q21, Q22, Q23, Q24, Q25, Q26, Q27, Q28, Q29, Q30, Q31, Q32, Q33, Q34, Q35, Q36, Q37, Q38, Q39, Q40, Q41, Q42, Q43, Q44, Q45, Q46, Q47, Q48, Q49, Q50, Q51, Q52, Q53, Q54, Q55, Q56, Q57, Q58]), "operationType" : NewBodyOperationType.REMOVE, "oppositeDirection" : true, "depth" : 50.8 * mm, "offsetDistance" : 25.4 * mm});
        }
        {
            var Q0;
            Q0=makeQuery(id+"F15.opExtrude","SWEPT_FACE",FACE,{"disambiguationData":[OSD([sQuery(id+"F14.wireOp",EDGE,"E24.left")])]});
            var sketch = newSketch(context, id + "F22", { "sketchPlane" : qUnion([Q0])});
            skLineSegment(sketch, "E33.bottom", {"start": v(3.18, -419.86) * mm, "end": v(47.63, -419.86) * mm});
            skLineSegment(sketch, "E33.top", {"start": v(3.18, -375.41) * mm, "end": v(47.63, -375.41) * mm});
            skLineSegment(sketch, "E33.left", {"start": v(3.18, -419.86) * mm, "end": v(3.18, -375.41) * mm});
            skLineSegment(sketch, "E33.right", {"start": v(47.63, -419.86) * mm, "end": v(47.63, -375.41) * mm});
            skPoint(sketch, "E33.middle", {"position": v(25.4, -397.64) * mm});
            skPoint(sketch, "E33.middle.positionSnap0", {"position": v(25.4, -372.24) * mm});
            skPoint(sketch, "E33.middle.positionSnap1", {"position": v(50.8, -397.64) * mm});
            skPoint(sketch, "E33.centerSnap0", {"position": v(25.4, -372.24) * mm});
            skPoint(sketch, "E33.centerSnap1", {"position": v(50.8, -397.64) * mm});
            skSolve(sketch);
        }
        {
            var Q0;
            Q0 = qSketchRegion(id + "F22", true);
            extrude(context, id + "F23", {"entities" : qUnion([Q0]), "operationType" : NewBodyOperationType.REMOVE, "oppositeDirection" : true, "depth" : 762 * mm, "offsetDistance" : 25.4 * mm});
        }
        {
            var Q0;
            Q0=makeQuery(id+"F1.opExtrude","CAP_FACE",FACE,{"disambiguationData":[OSD([sQuery(id+"F0.wireOp",EDGE,"E0.bottom"),sQuery(id+"F0.wireOp",EDGE,"E0.top"),sQuery(id+"F0.wireOp",EDGE,"E0.left"),sQuery(id+"F0.wireOp",EDGE,"E0.right")])],"isStart":true});
            var sketch = newSketch(context, id + "F24", { "sketchPlane" : qUnion([Q0])});
            skLineSegment(sketch, "E34.bottom", {"start": v(-4353.28, -485.52) * mm, "end": v(-3642.08, -485.52) * mm});
            skLineSegment(sketch, "E34.top", {"start": v(-4353.28, -460.12) * mm, "end": v(-3642.08, -460.12) * mm});
            skLineSegment(sketch, "E34.left", {"start": v(-4353.28, -485.52) * mm, "end": v(-4353.28, -460.12) * mm});
            skLineSegment(sketch, "E34.right", {"start": v(-3642.08, -485.52) * mm, "end": v(-3642.08, -460.12) * mm});
            skSolve(sketch);
        }
        {
            var Q0;
            Q0 = qSketchRegion(id + "F24", true);
            extrude(context, id + "F25", {"entities" : qUnion([Q0]), "depth" : 3.17 * mm, "offsetDistance" : 25.4 * mm});
        }
        {
            var Q0;
            Q0=makeQuery(id+"F25.opExtrude","CAP_FACE",FACE,{"disambiguationData":[OSD([sQuery(id+"F24.wireOp",EDGE,"E34.bottom"),sQuery(id+"F24.wireOp",EDGE,"E34.top"),sQuery(id+"F24.wireOp",EDGE,"E34.left"),sQuery(id+"F24.wireOp",EDGE,"E34.right")])],"isStart":false});
            var sketch = newSketch(context, id + "F26", { "sketchPlane" : qUnion([Q0])});
            skCircle(sketch, "E35", {"center": v(-4343.75, -472.82) * mm, "radius": 3.18 * mm});
            skPoint(sketch, "E35.centerSnap0", {"position": v(-4353.28, -472.82) * mm});
            skCircle(sketch, "E36", {"center": v(-4337.4, -472.82) * mm, "radius": 3.18 * mm});
            skLineSegment(sketch, "E37", {"start": v(-4343.75, -472.82) * mm, "end": v(-4337.4, -472.82) * mm});
            skLineSegment(sketch, "E38", {"start": v(-4343.75, -469.65) * mm, "end": v(-4337.4, -469.65) * mm});
            skLineSegment(sketch, "E39", {"start": v(-4337.4, -469.65) * mm, "end": v(-4337.4, -476) * mm});
            skLineSegment(sketch, "E40", {"start": v(-4337.4, -476) * mm, "end": v(-4343.75, -476) * mm});
            skLineSegment(sketch, "E41", {"start": v(-4343.75, -476) * mm, "end": v(-4343.75, -469.65) * mm});
            skCircle(sketch, "E42.1.0.0", {"center": v(-4318.35, -472.82) * mm, "radius": 3.18 * mm});
            skCircle(sketch, "E42.1.0.1", {"center": v(-4324.7, -472.82) * mm, "radius": 3.18 * mm});
            skLineSegment(sketch, "E42.1.0.2", {"start": v(-4324.7, -469.65) * mm, "end": v(-4318.35, -469.65) * mm});
            skLineSegment(sketch, "E42.1.0.3", {"start": v(-4318.35, -476) * mm, "end": v(-4324.7, -476) * mm});
            skCircle(sketch, "E42.2.0.0", {"center": v(-4299.3, -472.82) * mm, "radius": 3.18 * mm});
            skCircle(sketch, "E42.2.0.1", {"center": v(-4305.65, -472.82) * mm, "radius": 3.18 * mm});
            skLineSegment(sketch, "E42.2.0.2", {"start": v(-4305.65, -469.65) * mm, "end": v(-4299.3, -469.65) * mm});
            skLineSegment(sketch, "E42.2.0.3", {"start": v(-4299.3, -476) * mm, "end": v(-4305.65, -476) * mm});
            skCircle(sketch, "E42.3.0.0", {"center": v(-4280.25, -472.82) * mm, "radius": 3.18 * mm});
            skCircle(sketch, "E42.3.0.1", {"center": v(-4286.6, -472.82) * mm, "radius": 3.18 * mm});
            skLineSegment(sketch, "E42.3.0.2", {"start": v(-4286.6, -469.65) * mm, "end": v(-4280.25, -469.65) * mm});
            skLineSegment(sketch, "E42.3.0.3", {"start": v(-4280.25, -476) * mm, "end": v(-4286.6, -476) * mm});
            skCircle(sketch, "E42.4.0.0", {"center": v(-4261.2, -472.82) * mm, "radius": 3.18 * mm});
            skCircle(sketch, "E42.4.0.1", {"center": v(-4267.55, -472.82) * mm, "radius": 3.18 * mm});
            skLineSegment(sketch, "E42.4.0.2", {"start": v(-4267.55, -469.65) * mm, "end": v(-4261.2, -469.65) * mm});
            skLineSegment(sketch, "E42.4.0.3", {"start": v(-4261.2, -476) * mm, "end": v(-4267.55, -476) * mm});
            skCircle(sketch, "E42.5.0.0", {"center": v(-4242.15, -472.82) * mm, "radius": 3.18 * mm});
            skCircle(sketch, "E42.5.0.1", {"center": v(-4248.5, -472.82) * mm, "radius": 3.18 * mm});
            skLineSegment(sketch, "E42.5.0.2", {"start": v(-4248.5, -469.65) * mm, "end": v(-4242.15, -469.65) * mm});
            skLineSegment(sketch, "E42.5.0.3", {"start": v(-4242.15, -476) * mm, "end": v(-4248.5, -476) * mm});
            skCircle(sketch, "E42.6.0.0", {"center": v(-4223.1, -472.82) * mm, "radius": 3.18 * mm});
            skCircle(sketch, "E42.6.0.1", {"center": v(-4229.45, -472.82) * mm, "radius": 3.18 * mm});
            skLineSegment(sketch, "E42.6.0.2", {"start": v(-4229.45, -469.65) * mm, "end": v(-4223.1, -469.65) * mm});
            skLineSegment(sketch, "E42.6.0.3", {"start": v(-4223.1, -476) * mm, "end": v(-4229.45, -476) * mm});
            skCircle(sketch, "E42.7.0.0", {"center": v(-4204.05, -472.82) * mm, "radius": 3.18 * mm});
            skCircle(sketch, "E42.7.0.1", {"center": v(-4210.4, -472.82) * mm, "radius": 3.18 * mm});
            skLineSegment(sketch, "E42.7.0.2", {"start": v(-4210.4, -469.65) * mm, "end": v(-4204.05, -469.65) * mm});
            skLineSegment(sketch, "E42.7.0.3", {"start": v(-4204.05, -476) * mm, "end": v(-4210.4, -476) * mm});
            skCircle(sketch, "E42.8.0.0", {"center": v(-4185, -472.82) * mm, "radius": 3.18 * mm});
            skCircle(sketch, "E42.8.0.1", {"center": v(-4191.35, -472.82) * mm, "radius": 3.18 * mm});
            skLineSegment(sketch, "E42.8.0.2", {"start": v(-4191.35, -469.65) * mm, "end": v(-4185, -469.65) * mm});
            skLineSegment(sketch, "E42.8.0.3", {"start": v(-4185, -476) * mm, "end": v(-4191.35, -476) * mm});
            skCircle(sketch, "E42.9.0.0", {"center": v(-4165.95, -472.82) * mm, "radius": 3.18 * mm});
            skCircle(sketch, "E42.9.0.1", {"center": v(-4172.3, -472.82) * mm, "radius": 3.18 * mm});
            skLineSegment(sketch, "E42.9.0.2", {"start": v(-4172.3, -469.65) * mm, "end": v(-4165.95, -469.65) * mm});
            skLineSegment(sketch, "E42.9.0.3", {"start": v(-4165.95, -476) * mm, "end": v(-4172.3, -476) * mm});
            skCircle(sketch, "E42.10.0.0", {"center": v(-4146.9, -472.82) * mm, "radius": 3.18 * mm});
            skCircle(sketch, "E42.10.0.1", {"center": v(-4153.25, -472.82) * mm, "radius": 3.18 * mm});
            skLineSegment(sketch, "E42.10.0.2", {"start": v(-4153.25, -469.65) * mm, "end": v(-4146.9, -469.65) * mm});
            skLineSegment(sketch, "E42.10.0.3", {"start": v(-4146.9, -476) * mm, "end": v(-4153.25, -476) * mm});
            skCircle(sketch, "E42.11.0.0", {"center": v(-4127.85, -472.82) * mm, "radius": 3.18 * mm});
            skCircle(sketch, "E42.11.0.1", {"center": v(-4134.2, -472.82) * mm, "radius": 3.18 * mm});
            skLineSegment(sketch, "E42.11.0.2", {"start": v(-4134.2, -469.65) * mm, "end": v(-4127.85, -469.65) * mm});
            skLineSegment(sketch, "E42.11.0.3", {"start": v(-4127.85, -476) * mm, "end": v(-4134.2, -476) * mm});
            skCircle(sketch, "E42.12.0.0", {"center": v(-4108.8, -472.82) * mm, "radius": 3.18 * mm});
            skCircle(sketch, "E42.12.0.1", {"center": v(-4115.15, -472.82) * mm, "radius": 3.18 * mm});
            skLineSegment(sketch, "E42.12.0.2", {"start": v(-4115.15, -469.65) * mm, "end": v(-4108.8, -469.65) * mm});
            skLineSegment(sketch, "E42.12.0.3", {"start": v(-4108.8, -476) * mm, "end": v(-4115.15, -476) * mm});
            skCircle(sketch, "E42.13.0.0", {"center": v(-4089.75, -472.82) * mm, "radius": 3.18 * mm});
            skCircle(sketch, "E42.13.0.1", {"center": v(-4096.1, -472.82) * mm, "radius": 3.18 * mm});
            skLineSegment(sketch, "E42.13.0.2", {"start": v(-4096.1, -469.65) * mm, "end": v(-4089.75, -469.65) * mm});
            skLineSegment(sketch, "E42.13.0.3", {"start": v(-4089.75, -476) * mm, "end": v(-4096.1, -476) * mm});
            skCircle(sketch, "E42.14.0.0", {"center": v(-4070.7, -472.82) * mm, "radius": 3.18 * mm});
            skCircle(sketch, "E42.14.0.1", {"center": v(-4077.05, -472.82) * mm, "radius": 3.18 * mm});
            skLineSegment(sketch, "E42.14.0.2", {"start": v(-4077.05, -469.65) * mm, "end": v(-4070.7, -469.65) * mm});
            skLineSegment(sketch, "E42.14.0.3", {"start": v(-4070.7, -476) * mm, "end": v(-4077.05, -476) * mm});
            skCircle(sketch, "E42.15.0.0", {"center": v(-4051.65, -472.82) * mm, "radius": 3.18 * mm});
            skCircle(sketch, "E42.15.0.1", {"center": v(-4058, -472.82) * mm, "radius": 3.18 * mm});
            skLineSegment(sketch, "E42.15.0.2", {"start": v(-4058, -469.65) * mm, "end": v(-4051.65, -469.65) * mm});
            skLineSegment(sketch, "E42.15.0.3", {"start": v(-4051.65, -476) * mm, "end": v(-4058, -476) * mm});
            skCircle(sketch, "E42.16.0.0", {"center": v(-4032.6, -472.82) * mm, "radius": 3.18 * mm});
            skCircle(sketch, "E42.16.0.1", {"center": v(-4038.95, -472.82) * mm, "radius": 3.18 * mm});
            skLineSegment(sketch, "E42.16.0.2", {"start": v(-4038.95, -469.65) * mm, "end": v(-4032.6, -469.65) * mm});
            skLineSegment(sketch, "E42.16.0.3", {"start": v(-4032.6, -476) * mm, "end": v(-4038.95, -476) * mm});
            skCircle(sketch, "E42.17.0.0", {"center": v(-4013.55, -472.82) * mm, "radius": 3.18 * mm});
            skCircle(sketch, "E42.17.0.1", {"center": v(-4019.9, -472.82) * mm, "radius": 3.18 * mm});
            skLineSegment(sketch, "E42.17.0.2", {"start": v(-4019.9, -469.65) * mm, "end": v(-4013.55, -469.65) * mm});
            skLineSegment(sketch, "E42.17.0.3", {"start": v(-4013.55, -476) * mm, "end": v(-4019.9, -476) * mm});
            skCircle(sketch, "E42.18.0.0", {"center": v(-3994.5, -472.82) * mm, "radius": 3.18 * mm});
            skCircle(sketch, "E42.18.0.1", {"center": v(-4000.85, -472.82) * mm, "radius": 3.18 * mm});
            skLineSegment(sketch, "E42.18.0.2", {"start": v(-4000.85, -469.65) * mm, "end": v(-3994.5, -469.65) * mm});
            skLineSegment(sketch, "E42.18.0.3", {"start": v(-3994.5, -476) * mm, "end": v(-4000.85, -476) * mm});
            skCircle(sketch, "E42.19.0.0", {"center": v(-3975.45, -472.82) * mm, "radius": 3.18 * mm});
            skCircle(sketch, "E42.19.0.1", {"center": v(-3981.8, -472.82) * mm, "radius": 3.18 * mm});
            skLineSegment(sketch, "E42.19.0.2", {"start": v(-3981.8, -469.65) * mm, "end": v(-3975.45, -469.65) * mm});
            skLineSegment(sketch, "E42.19.0.3", {"start": v(-3975.45, -476) * mm, "end": v(-3981.8, -476) * mm});
            skCircle(sketch, "E42.20.0.0", {"center": v(-3956.4, -472.82) * mm, "radius": 3.18 * mm});
            skCircle(sketch, "E42.20.0.1", {"center": v(-3962.75, -472.82) * mm, "radius": 3.18 * mm});
            skLineSegment(sketch, "E42.20.0.2", {"start": v(-3962.75, -469.65) * mm, "end": v(-3956.4, -469.65) * mm});
            skLineSegment(sketch, "E42.20.0.3", {"start": v(-3956.4, -476) * mm, "end": v(-3962.75, -476) * mm});
            skCircle(sketch, "E42.21.0.0", {"center": v(-3937.35, -472.82) * mm, "radius": 3.18 * mm});
            skCircle(sketch, "E42.21.0.1", {"center": v(-3943.7, -472.82) * mm, "radius": 3.18 * mm});
            skLineSegment(sketch, "E42.21.0.2", {"start": v(-3943.7, -469.65) * mm, "end": v(-3937.35, -469.65) * mm});
            skLineSegment(sketch, "E42.21.0.3", {"start": v(-3937.35, -476) * mm, "end": v(-3943.7, -476) * mm});
            skCircle(sketch, "E42.22.0.0", {"center": v(-3918.3, -472.82) * mm, "radius": 3.18 * mm});
            skCircle(sketch, "E42.22.0.1", {"center": v(-3924.65, -472.82) * mm, "radius": 3.18 * mm});
            skLineSegment(sketch, "E42.22.0.2", {"start": v(-3924.65, -469.65) * mm, "end": v(-3918.3, -469.65) * mm});
            skLineSegment(sketch, "E42.22.0.3", {"start": v(-3918.3, -476) * mm, "end": v(-3924.65, -476) * mm});
            skCircle(sketch, "E42.23.0.0", {"center": v(-3899.25, -472.82) * mm, "radius": 3.18 * mm});
            skCircle(sketch, "E42.23.0.1", {"center": v(-3905.6, -472.82) * mm, "radius": 3.18 * mm});
            skLineSegment(sketch, "E42.23.0.2", {"start": v(-3905.6, -469.65) * mm, "end": v(-3899.25, -469.65) * mm});
            skLineSegment(sketch, "E42.23.0.3", {"start": v(-3899.25, -476) * mm, "end": v(-3905.6, -476) * mm});
            skCircle(sketch, "E42.24.0.0", {"center": v(-3880.2, -472.82) * mm, "radius": 3.18 * mm});
            skCircle(sketch, "E42.24.0.1", {"center": v(-3886.55, -472.82) * mm, "radius": 3.18 * mm});
            skLineSegment(sketch, "E42.24.0.2", {"start": v(-3886.55, -469.65) * mm, "end": v(-3880.2, -469.65) * mm});
            skLineSegment(sketch, "E42.24.0.3", {"start": v(-3880.2, -476) * mm, "end": v(-3886.55, -476) * mm});
            skCircle(sketch, "E42.25.0.0", {"center": v(-3861.15, -472.82) * mm, "radius": 3.18 * mm});
            skCircle(sketch, "E42.25.0.1", {"center": v(-3867.5, -472.82) * mm, "radius": 3.18 * mm});
            skLineSegment(sketch, "E42.25.0.2", {"start": v(-3867.5, -469.65) * mm, "end": v(-3861.15, -469.65) * mm});
            skLineSegment(sketch, "E42.25.0.3", {"start": v(-3861.15, -476) * mm, "end": v(-3867.5, -476) * mm});
            skCircle(sketch, "E42.26.0.0", {"center": v(-3842.1, -472.82) * mm, "radius": 3.18 * mm});
            skCircle(sketch, "E42.26.0.1", {"center": v(-3848.45, -472.82) * mm, "radius": 3.18 * mm});
            skLineSegment(sketch, "E42.26.0.2", {"start": v(-3848.45, -469.65) * mm, "end": v(-3842.1, -469.65) * mm});
            skLineSegment(sketch, "E42.26.0.3", {"start": v(-3842.1, -476) * mm, "end": v(-3848.45, -476) * mm});
            skCircle(sketch, "E42.27.0.0", {"center": v(-3823.05, -472.82) * mm, "radius": 3.18 * mm});
            skCircle(sketch, "E42.27.0.1", {"center": v(-3829.4, -472.82) * mm, "radius": 3.18 * mm});
            skLineSegment(sketch, "E42.27.0.2", {"start": v(-3829.4, -469.65) * mm, "end": v(-3823.05, -469.65) * mm});
            skLineSegment(sketch, "E42.27.0.3", {"start": v(-3823.05, -476) * mm, "end": v(-3829.4, -476) * mm});
            skCircle(sketch, "E42.28.0.0", {"center": v(-3804, -472.82) * mm, "radius": 3.18 * mm});
            skCircle(sketch, "E42.28.0.1", {"center": v(-3810.35, -472.82) * mm, "radius": 3.18 * mm});
            skLineSegment(sketch, "E42.28.0.2", {"start": v(-3810.35, -469.65) * mm, "end": v(-3804, -469.65) * mm});
            skLineSegment(sketch, "E42.28.0.3", {"start": v(-3804, -476) * mm, "end": v(-3810.35, -476) * mm});
            skCircle(sketch, "E42.29.0.0", {"center": v(-3784.95, -472.82) * mm, "radius": 3.18 * mm});
            skCircle(sketch, "E42.29.0.1", {"center": v(-3791.3, -472.82) * mm, "radius": 3.18 * mm});
            skLineSegment(sketch, "E42.29.0.2", {"start": v(-3791.3, -469.65) * mm, "end": v(-3784.95, -469.65) * mm});
            skLineSegment(sketch, "E42.29.0.3", {"start": v(-3784.95, -476) * mm, "end": v(-3791.3, -476) * mm});
            skCircle(sketch, "E42.30.0.0", {"center": v(-3765.9, -472.82) * mm, "radius": 3.18 * mm});
            skCircle(sketch, "E42.30.0.1", {"center": v(-3772.25, -472.82) * mm, "radius": 3.18 * mm});
            skLineSegment(sketch, "E42.30.0.2", {"start": v(-3772.25, -469.65) * mm, "end": v(-3765.9, -469.65) * mm});
            skLineSegment(sketch, "E42.30.0.3", {"start": v(-3765.9, -476) * mm, "end": v(-3772.25, -476) * mm});
            skCircle(sketch, "E42.31.0.0", {"center": v(-3746.85, -472.82) * mm, "radius": 3.18 * mm});
            skCircle(sketch, "E42.31.0.1", {"center": v(-3753.2, -472.82) * mm, "radius": 3.18 * mm});
            skLineSegment(sketch, "E42.31.0.2", {"start": v(-3753.2, -469.65) * mm, "end": v(-3746.85, -469.65) * mm});
            skLineSegment(sketch, "E42.31.0.3", {"start": v(-3746.85, -476) * mm, "end": v(-3753.2, -476) * mm});
            skCircle(sketch, "E42.32.0.0", {"center": v(-3727.8, -472.82) * mm, "radius": 3.18 * mm});
            skCircle(sketch, "E42.32.0.1", {"center": v(-3734.15, -472.82) * mm, "radius": 3.18 * mm});
            skLineSegment(sketch, "E42.32.0.2", {"start": v(-3734.15, -469.65) * mm, "end": v(-3727.8, -469.65) * mm});
            skLineSegment(sketch, "E42.32.0.3", {"start": v(-3727.8, -476) * mm, "end": v(-3734.15, -476) * mm});
            skCircle(sketch, "E42.33.0.0", {"center": v(-3708.75, -472.82) * mm, "radius": 3.18 * mm});
            skCircle(sketch, "E42.33.0.1", {"center": v(-3715.1, -472.82) * mm, "radius": 3.18 * mm});
            skLineSegment(sketch, "E42.33.0.2", {"start": v(-3715.1, -469.65) * mm, "end": v(-3708.75, -469.65) * mm});
            skLineSegment(sketch, "E42.33.0.3", {"start": v(-3708.75, -476) * mm, "end": v(-3715.1, -476) * mm});
            skCircle(sketch, "E42.34.0.0", {"center": v(-3689.7, -472.82) * mm, "radius": 3.18 * mm});
            skCircle(sketch, "E42.34.0.1", {"center": v(-3696.05, -472.82) * mm, "radius": 3.18 * mm});
            skLineSegment(sketch, "E42.34.0.2", {"start": v(-3696.05, -469.65) * mm, "end": v(-3689.7, -469.65) * mm});
            skLineSegment(sketch, "E42.34.0.3", {"start": v(-3689.7, -476) * mm, "end": v(-3696.05, -476) * mm});
            skCircle(sketch, "E42.35.0.0", {"center": v(-3670.65, -472.82) * mm, "radius": 3.18 * mm});
            skCircle(sketch, "E42.35.0.1", {"center": v(-3677, -472.82) * mm, "radius": 3.18 * mm});
            skLineSegment(sketch, "E42.35.0.2", {"start": v(-3677, -469.65) * mm, "end": v(-3670.65, -469.65) * mm});
            skLineSegment(sketch, "E42.35.0.3", {"start": v(-3670.65, -476) * mm, "end": v(-3677, -476) * mm});
            skCircle(sketch, "E42.36.0.0", {"center": v(-3651.6, -472.82) * mm, "radius": 3.18 * mm});
            skCircle(sketch, "E42.36.0.1", {"center": v(-3657.95, -472.82) * mm, "radius": 3.18 * mm});
            skLineSegment(sketch, "E42.36.0.2", {"start": v(-3657.95, -469.65) * mm, "end": v(-3651.6, -469.65) * mm});
            skLineSegment(sketch, "E42.36.0.3", {"start": v(-3651.6, -476) * mm, "end": v(-3657.95, -476) * mm});
            skLineSegment(sketch, "E42.direction1", {"start": v(-4337.4, -472.82) * mm, "end": v(-4318.35, -472.82) * mm, "construction": true});
            skSolve(sketch);
        }
        {
            var Q0;
            Q0 = qSketchRegion(id + "F26", true);
            extrude(context, id + "F27", {"entities" : qUnion([Q0]), "operationType" : NewBodyOperationType.REMOVE, "oppositeDirection" : true, "depth" : 25.4 * mm, "offsetDistance" : 25.4 * mm});
        }
        {
            var Q0;
            Q0=makeQuery(id+"F25.opExtrude","CAP_FACE",FACE,{"disambiguationData":[OSD([sQuery(id+"F24.wireOp",EDGE,"E34.bottom"),sQuery(id+"F24.wireOp",EDGE,"E34.top"),sQuery(id+"F24.wireOp",EDGE,"E34.left"),sQuery(id+"F24.wireOp",EDGE,"E34.right")])],"isStart":false});
            var sketch = newSketch(context, id + "F28", { "sketchPlane" : qUnion([Q0])});
            skLineSegment(sketch, "E43", {"start": v(-4353.28, -495.78) * mm, "end": v(-4309.05, -495.78) * mm});
            skLineSegment(sketch, "E44.bottom", {"start": v(-4353.28, -485.52) * mm, "end": v(-3851.63, -485.52) * mm});
            skLineSegment(sketch, "E44.top", {"start": v(-4353.28, -460.12) * mm, "end": v(-3851.63, -460.12) * mm});
            skLineSegment(sketch, "E44.left", {"start": v(-4353.28, -485.52) * mm, "end": v(-4353.28, -460.12) * mm});
            skLineSegment(sketch, "E44.right", {"start": v(-3851.63, -485.52) * mm, "end": v(-3851.63, -460.12) * mm});
            skLineSegment(sketch, "E45.MirrorCS", {"start": v(-4353.28, -506.03) * mm, "end": v(-3851.63, -506.03) * mm});
            skLineSegment(sketch, "E46.MirrorCS", {"start": v(-4353.28, -506.03) * mm, "end": v(-4353.28, -531.43) * mm});
            skLineSegment(sketch, "E47.MirrorCS", {"start": v(-4353.28, -531.43) * mm, "end": v(-3851.63, -531.43) * mm});
            skLineSegment(sketch, "E48.MirrorCS", {"start": v(-3851.63, -506.03) * mm, "end": v(-3851.63, -531.43) * mm});
            skSolve(sketch);
        }
        {
            var Q0;
            Q0=makeQuery(id+"F28.imprint","IMPRINT",FACE,{"disambiguationData":[TD([[makeQuery(id+"F28.imprint","IMPRINT",EDGE,{"derivedFrom":sQuery(id+"F28.wireOp",EDGE,"E45.MirrorCS")}),-1.0]])]});
            extrude(context, id + "F29", {"entities" : qUnion([Q0]), "oppositeDirection" : true, "depth" : 3.17 * mm, "offsetDistance" : 25.4 * mm});
        }
        {
            var Q0;
            Q0=makeQuery(id+"F29.opExtrude","CAP_FACE",FACE,{"disambiguationData":[OSD([sQuery(id+"F28.wireOp",EDGE,"E45.MirrorCS"),sQuery(id+"F28.wireOp",EDGE,"E46.MirrorCS"),sQuery(id+"F28.wireOp",EDGE,"E47.MirrorCS"),sQuery(id+"F28.wireOp",EDGE,"E48.MirrorCS")])],"isStart":true});
            var sketch = newSketch(context, id + "F30", { "sketchPlane" : qUnion([Q0])});
            skCircle(sketch, "E49", {"center": v(-4343.75, -518.73) * mm, "radius": 3.18 * mm});
            skPoint(sketch, "E49.centerSnap0", {"position": v(-4353.28, -518.73) * mm});
            skCircle(sketch, "E50", {"center": v(-4337.4, -518.73) * mm, "radius": 3.18 * mm});
            skLineSegment(sketch, "E51", {"start": v(-4343.75, -515.56) * mm, "end": v(-4337.4, -515.56) * mm});
            skLineSegment(sketch, "E52", {"start": v(-4343.75, -521.9) * mm, "end": v(-4337.4, -521.9) * mm});
            skCircle(sketch, "E53.1.0.0", {"center": v(-4318.35, -518.73) * mm, "radius": 3.18 * mm});
            skCircle(sketch, "E53.1.0.1", {"center": v(-4324.7, -518.73) * mm, "radius": 3.18 * mm});
            skLineSegment(sketch, "E53.1.0.2", {"start": v(-4324.7, -515.56) * mm, "end": v(-4318.35, -515.56) * mm});
            skLineSegment(sketch, "E53.1.0.3", {"start": v(-4324.7, -521.9) * mm, "end": v(-4318.35, -521.9) * mm});
            skCircle(sketch, "E53.2.0.0", {"center": v(-4299.3, -518.73) * mm, "radius": 3.18 * mm});
            skCircle(sketch, "E53.2.0.1", {"center": v(-4305.65, -518.73) * mm, "radius": 3.18 * mm});
            skLineSegment(sketch, "E53.2.0.2", {"start": v(-4305.65, -515.56) * mm, "end": v(-4299.3, -515.56) * mm});
            skLineSegment(sketch, "E53.2.0.3", {"start": v(-4305.65, -521.9) * mm, "end": v(-4299.3, -521.9) * mm});
            skCircle(sketch, "E53.3.0.0", {"center": v(-4280.25, -518.73) * mm, "radius": 3.18 * mm});
            skCircle(sketch, "E53.3.0.1", {"center": v(-4286.6, -518.73) * mm, "radius": 3.18 * mm});
            skLineSegment(sketch, "E53.3.0.2", {"start": v(-4286.6, -515.56) * mm, "end": v(-4280.25, -515.56) * mm});
            skLineSegment(sketch, "E53.3.0.3", {"start": v(-4286.6, -521.9) * mm, "end": v(-4280.25, -521.9) * mm});
            skCircle(sketch, "E53.4.0.0", {"center": v(-4261.2, -518.73) * mm, "radius": 3.18 * mm});
            skCircle(sketch, "E53.4.0.1", {"center": v(-4267.55, -518.73) * mm, "radius": 3.18 * mm});
            skLineSegment(sketch, "E53.4.0.2", {"start": v(-4267.55, -515.56) * mm, "end": v(-4261.2, -515.56) * mm});
            skLineSegment(sketch, "E53.4.0.3", {"start": v(-4267.55, -521.9) * mm, "end": v(-4261.2, -521.9) * mm});
            skCircle(sketch, "E53.5.0.0", {"center": v(-4242.15, -518.73) * mm, "radius": 3.18 * mm});
            skCircle(sketch, "E53.5.0.1", {"center": v(-4248.5, -518.73) * mm, "radius": 3.18 * mm});
            skLineSegment(sketch, "E53.5.0.2", {"start": v(-4248.5, -515.56) * mm, "end": v(-4242.15, -515.56) * mm});
            skLineSegment(sketch, "E53.5.0.3", {"start": v(-4248.5, -521.9) * mm, "end": v(-4242.15, -521.9) * mm});
            skCircle(sketch, "E53.6.0.0", {"center": v(-4223.1, -518.73) * mm, "radius": 3.18 * mm});
            skCircle(sketch, "E53.6.0.1", {"center": v(-4229.45, -518.73) * mm, "radius": 3.18 * mm});
            skLineSegment(sketch, "E53.6.0.2", {"start": v(-4229.45, -515.56) * mm, "end": v(-4223.1, -515.56) * mm});
            skLineSegment(sketch, "E53.6.0.3", {"start": v(-4229.45, -521.9) * mm, "end": v(-4223.1, -521.9) * mm});
            skCircle(sketch, "E53.7.0.0", {"center": v(-4204.05, -518.73) * mm, "radius": 3.18 * mm});
            skCircle(sketch, "E53.7.0.1", {"center": v(-4210.4, -518.73) * mm, "radius": 3.18 * mm});
            skLineSegment(sketch, "E53.7.0.2", {"start": v(-4210.4, -515.56) * mm, "end": v(-4204.05, -515.56) * mm});
            skLineSegment(sketch, "E53.7.0.3", {"start": v(-4210.4, -521.9) * mm, "end": v(-4204.05, -521.9) * mm});
            skCircle(sketch, "E53.8.0.0", {"center": v(-4185, -518.73) * mm, "radius": 3.18 * mm});
            skCircle(sketch, "E53.8.0.1", {"center": v(-4191.35, -518.73) * mm, "radius": 3.18 * mm});
            skLineSegment(sketch, "E53.8.0.2", {"start": v(-4191.35, -515.56) * mm, "end": v(-4185, -515.56) * mm});
            skLineSegment(sketch, "E53.8.0.3", {"start": v(-4191.35, -521.9) * mm, "end": v(-4185, -521.9) * mm});
            skCircle(sketch, "E53.9.0.0", {"center": v(-4165.95, -518.73) * mm, "radius": 3.18 * mm});
            skCircle(sketch, "E53.9.0.1", {"center": v(-4172.3, -518.73) * mm, "radius": 3.18 * mm});
            skLineSegment(sketch, "E53.9.0.2", {"start": v(-4172.3, -515.56) * mm, "end": v(-4165.95, -515.56) * mm});
            skLineSegment(sketch, "E53.9.0.3", {"start": v(-4172.3, -521.9) * mm, "end": v(-4165.95, -521.9) * mm});
            skCircle(sketch, "E53.10.0.0", {"center": v(-4146.9, -518.73) * mm, "radius": 3.18 * mm});
            skCircle(sketch, "E53.10.0.1", {"center": v(-4153.25, -518.73) * mm, "radius": 3.18 * mm});
            skLineSegment(sketch, "E53.10.0.2", {"start": v(-4153.25, -515.56) * mm, "end": v(-4146.9, -515.56) * mm});
            skLineSegment(sketch, "E53.10.0.3", {"start": v(-4153.25, -521.9) * mm, "end": v(-4146.9, -521.9) * mm});
            skCircle(sketch, "E53.11.0.0", {"center": v(-4127.85, -518.73) * mm, "radius": 3.18 * mm});
            skCircle(sketch, "E53.11.0.1", {"center": v(-4134.2, -518.73) * mm, "radius": 3.18 * mm});
            skLineSegment(sketch, "E53.11.0.2", {"start": v(-4134.2, -515.56) * mm, "end": v(-4127.85, -515.56) * mm});
            skLineSegment(sketch, "E53.11.0.3", {"start": v(-4134.2, -521.9) * mm, "end": v(-4127.85, -521.9) * mm});
            skCircle(sketch, "E53.12.0.0", {"center": v(-4108.8, -518.73) * mm, "radius": 3.18 * mm});
            skCircle(sketch, "E53.12.0.1", {"center": v(-4115.15, -518.73) * mm, "radius": 3.18 * mm});
            skLineSegment(sketch, "E53.12.0.2", {"start": v(-4115.15, -515.56) * mm, "end": v(-4108.8, -515.56) * mm});
            skLineSegment(sketch, "E53.12.0.3", {"start": v(-4115.15, -521.9) * mm, "end": v(-4108.8, -521.9) * mm});
            skCircle(sketch, "E53.13.0.0", {"center": v(-4089.75, -518.73) * mm, "radius": 3.18 * mm});
            skCircle(sketch, "E53.13.0.1", {"center": v(-4096.1, -518.73) * mm, "radius": 3.18 * mm});
            skLineSegment(sketch, "E53.13.0.2", {"start": v(-4096.1, -515.56) * mm, "end": v(-4089.75, -515.56) * mm});
            skLineSegment(sketch, "E53.13.0.3", {"start": v(-4096.1, -521.9) * mm, "end": v(-4089.75, -521.9) * mm});
            skCircle(sketch, "E53.14.0.0", {"center": v(-4070.7, -518.73) * mm, "radius": 3.18 * mm});
            skCircle(sketch, "E53.14.0.1", {"center": v(-4077.05, -518.73) * mm, "radius": 3.18 * mm});
            skLineSegment(sketch, "E53.14.0.2", {"start": v(-4077.05, -515.56) * mm, "end": v(-4070.7, -515.56) * mm});
            skLineSegment(sketch, "E53.14.0.3", {"start": v(-4077.05, -521.9) * mm, "end": v(-4070.7, -521.9) * mm});
            skCircle(sketch, "E53.15.0.0", {"center": v(-4051.65, -518.73) * mm, "radius": 3.18 * mm});
            skCircle(sketch, "E53.15.0.1", {"center": v(-4058, -518.73) * mm, "radius": 3.18 * mm});
            skLineSegment(sketch, "E53.15.0.2", {"start": v(-4058, -515.56) * mm, "end": v(-4051.65, -515.56) * mm});
            skLineSegment(sketch, "E53.15.0.3", {"start": v(-4058, -521.9) * mm, "end": v(-4051.65, -521.9) * mm});
            skCircle(sketch, "E53.16.0.0", {"center": v(-4032.6, -518.73) * mm, "radius": 3.18 * mm});
            skCircle(sketch, "E53.16.0.1", {"center": v(-4038.95, -518.73) * mm, "radius": 3.18 * mm});
            skLineSegment(sketch, "E53.16.0.2", {"start": v(-4038.95, -515.56) * mm, "end": v(-4032.6, -515.56) * mm});
            skLineSegment(sketch, "E53.16.0.3", {"start": v(-4038.95, -521.9) * mm, "end": v(-4032.6, -521.9) * mm});
            skCircle(sketch, "E53.17.0.0", {"center": v(-4013.55, -518.73) * mm, "radius": 3.18 * mm});
            skCircle(sketch, "E53.17.0.1", {"center": v(-4019.9, -518.73) * mm, "radius": 3.18 * mm});
            skLineSegment(sketch, "E53.17.0.2", {"start": v(-4019.9, -515.56) * mm, "end": v(-4013.55, -515.56) * mm});
            skLineSegment(sketch, "E53.17.0.3", {"start": v(-4019.9, -521.9) * mm, "end": v(-4013.55, -521.9) * mm});
            skCircle(sketch, "E53.18.0.0", {"center": v(-3994.5, -518.73) * mm, "radius": 3.18 * mm});
            skCircle(sketch, "E53.18.0.1", {"center": v(-4000.85, -518.73) * mm, "radius": 3.18 * mm});
            skLineSegment(sketch, "E53.18.0.2", {"start": v(-4000.85, -515.56) * mm, "end": v(-3994.5, -515.56) * mm});
            skLineSegment(sketch, "E53.18.0.3", {"start": v(-4000.85, -521.9) * mm, "end": v(-3994.5, -521.9) * mm});
            skCircle(sketch, "E53.19.0.0", {"center": v(-3975.45, -518.73) * mm, "radius": 3.18 * mm});
            skCircle(sketch, "E53.19.0.1", {"center": v(-3981.8, -518.73) * mm, "radius": 3.18 * mm});
            skLineSegment(sketch, "E53.19.0.2", {"start": v(-3981.8, -515.56) * mm, "end": v(-3975.45, -515.56) * mm});
            skLineSegment(sketch, "E53.19.0.3", {"start": v(-3981.8, -521.9) * mm, "end": v(-3975.45, -521.9) * mm});
            skCircle(sketch, "E53.20.0.0", {"center": v(-3956.4, -518.73) * mm, "radius": 3.18 * mm});
            skCircle(sketch, "E53.20.0.1", {"center": v(-3962.75, -518.73) * mm, "radius": 3.18 * mm});
            skLineSegment(sketch, "E53.20.0.2", {"start": v(-3962.75, -515.56) * mm, "end": v(-3956.4, -515.56) * mm});
            skLineSegment(sketch, "E53.20.0.3", {"start": v(-3962.75, -521.9) * mm, "end": v(-3956.4, -521.9) * mm});
            skCircle(sketch, "E53.21.0.0", {"center": v(-3937.35, -518.73) * mm, "radius": 3.18 * mm});
            skCircle(sketch, "E53.21.0.1", {"center": v(-3943.7, -518.73) * mm, "radius": 3.18 * mm});
            skLineSegment(sketch, "E53.21.0.2", {"start": v(-3943.7, -515.56) * mm, "end": v(-3937.35, -515.56) * mm});
            skLineSegment(sketch, "E53.21.0.3", {"start": v(-3943.7, -521.9) * mm, "end": v(-3937.35, -521.9) * mm});
            skCircle(sketch, "E53.22.0.0", {"center": v(-3918.3, -518.73) * mm, "radius": 3.18 * mm});
            skCircle(sketch, "E53.22.0.1", {"center": v(-3924.65, -518.73) * mm, "radius": 3.18 * mm});
            skLineSegment(sketch, "E53.22.0.2", {"start": v(-3924.65, -515.56) * mm, "end": v(-3918.3, -515.56) * mm});
            skLineSegment(sketch, "E53.22.0.3", {"start": v(-3924.65, -521.9) * mm, "end": v(-3918.3, -521.9) * mm});
            skCircle(sketch, "E53.23.0.0", {"center": v(-3899.25, -518.73) * mm, "radius": 3.18 * mm});
            skCircle(sketch, "E53.23.0.1", {"center": v(-3905.6, -518.73) * mm, "radius": 3.18 * mm});
            skLineSegment(sketch, "E53.23.0.2", {"start": v(-3905.6, -515.56) * mm, "end": v(-3899.25, -515.56) * mm});
            skLineSegment(sketch, "E53.23.0.3", {"start": v(-3905.6, -521.9) * mm, "end": v(-3899.25, -521.9) * mm});
            skCircle(sketch, "E53.24.0.0", {"center": v(-3880.2, -518.73) * mm, "radius": 3.18 * mm});
            skCircle(sketch, "E53.24.0.1", {"center": v(-3886.55, -518.73) * mm, "radius": 3.18 * mm});
            skLineSegment(sketch, "E53.24.0.2", {"start": v(-3886.55, -515.56) * mm, "end": v(-3880.2, -515.56) * mm});
            skLineSegment(sketch, "E53.24.0.3", {"start": v(-3886.55, -521.9) * mm, "end": v(-3880.2, -521.9) * mm});
            skCircle(sketch, "E53.25.0.0", {"center": v(-3861.15, -518.73) * mm, "radius": 3.18 * mm});
            skCircle(sketch, "E53.25.0.1", {"center": v(-3867.5, -518.73) * mm, "radius": 3.18 * mm});
            skLineSegment(sketch, "E53.25.0.2", {"start": v(-3867.5, -515.56) * mm, "end": v(-3861.15, -515.56) * mm});
            skLineSegment(sketch, "E53.25.0.3", {"start": v(-3867.5, -521.9) * mm, "end": v(-3861.15, -521.9) * mm});
            skLineSegment(sketch, "E53.direction1", {"start": v(-4337.4, -518.73) * mm, "end": v(-4318.35, -518.73) * mm, "construction": true});
            skSolve(sketch);
        }
        {
            var Q0;
            Q0 = qSketchRegion(id + "F30", true);
            extrude(context, id + "F31", {"entities" : qUnion([Q0]), "operationType" : NewBodyOperationType.REMOVE, "oppositeDirection" : true, "depth" : 25.4 * mm, "offsetDistance" : 25.4 * mm});
        }
    });
